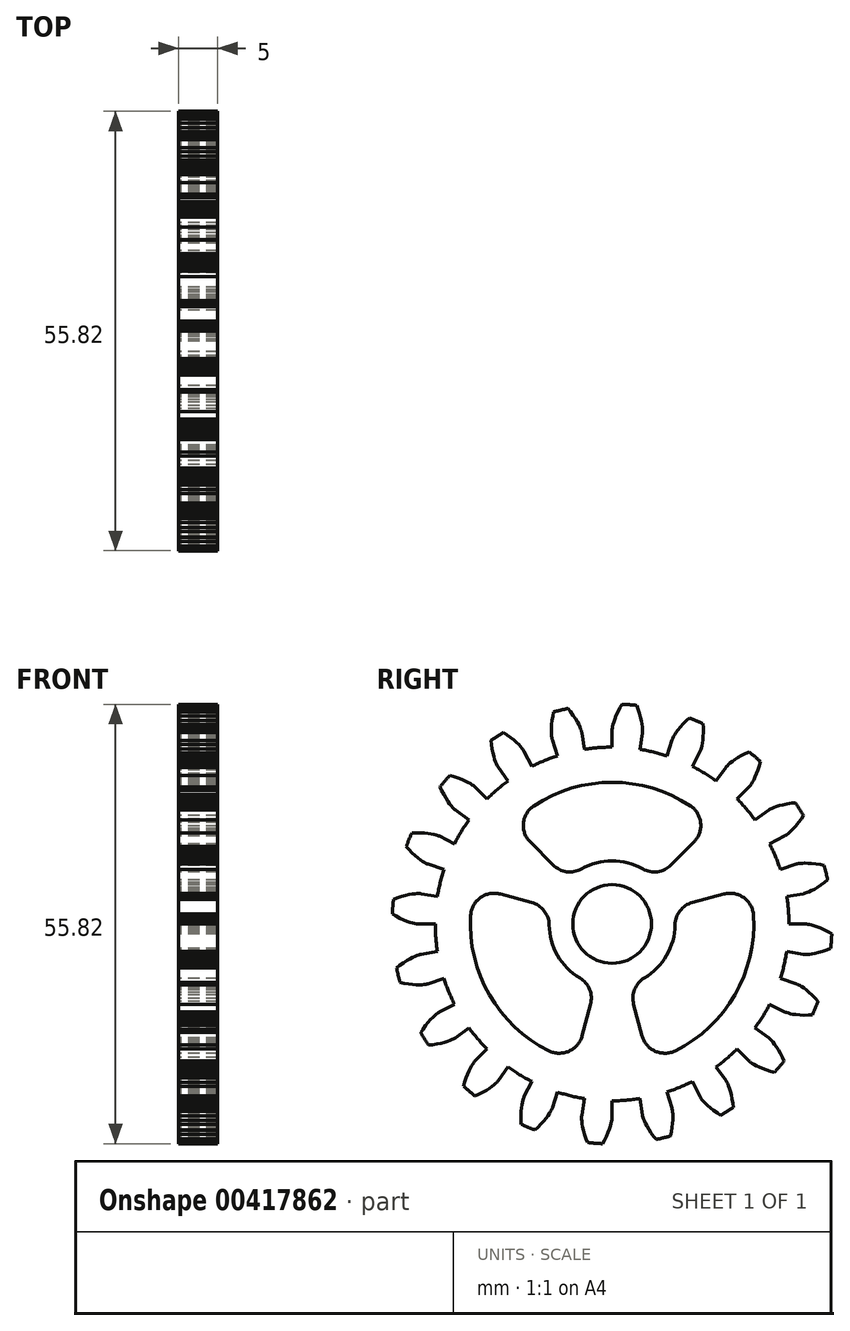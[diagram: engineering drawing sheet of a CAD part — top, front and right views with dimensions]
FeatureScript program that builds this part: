
annotation { "Feature Type Name" : "Feature", "Feature Type Description" : "" }
export const myFeature = defineFeature(function(context is Context, id is Id, definition is map)
    precondition{}
    {
        {
            assignVariable(context, id + "F0", {"name" : "GearThickness", "anyValue" : 5});
        }
        {
            var Q0;
            Q0=qCreatedBy(makeId("Right.planeOp"),FACE);
            var sketch = newSketch(context, id + "F1", { "sketchPlane" : qUnion([Q0])});
            skCircle(sketch, "E0", {"center": v(0, 0) * mm, "radius": 22.46 * mm});
            skCircle(sketch, "E1", {"center": v(0, 0) * mm, "radius": 24.6 * mm, "construction": true});
            skCircle(sketch, "E2", {"center": v(0, 0) * mm, "radius": 25.4 * mm, "construction": true});
            skCircle(sketch, "E3", {"center": v(0, 0) * mm, "radius": 27.94 * mm});
            skLineSegment(sketch, "E4", {"start": v(0, 0) * mm, "end": v(-24.6, 0) * mm, "construction": true});
            skLineSegment(sketch, "E5.1.0", {"start": v(0, 0) * mm, "end": v(-24.56, 1.23) * mm, "construction": true});
            skLineSegment(sketch, "E5.2.0", {"start": v(0, 0) * mm, "end": v(-24.47, 2.45) * mm, "construction": true});
            skLineSegment(sketch, "E5.3.0", {"start": v(0, 0) * mm, "end": v(-24.31, 3.67) * mm, "construction": true});
            skLineSegment(sketch, "E5.4.0", {"start": v(0, 0) * mm, "end": v(-24.1, 4.89) * mm, "construction": true});
            skLineSegment(sketch, "E5.5.0", {"start": v(0, 0) * mm, "end": v(-23.83, 6.08) * mm, "construction": true});
            skLineSegment(sketch, "E5.6.0", {"start": v(0, 0) * mm, "end": v(-23.5, 7.27) * mm, "construction": true});
            skLineSegment(sketch, "E5.7.0", {"start": v(0, 0) * mm, "end": v(-23.1, 8.43) * mm, "construction": true});
            skLineSegment(sketch, "E5.8.0", {"start": v(0, 0) * mm, "end": v(-22.65, 9.58) * mm, "construction": true});
            skLineSegment(sketch, "E5.9.0", {"start": v(0, 0) * mm, "end": v(-22.14, 10.7) * mm, "construction": true});
            skLineSegment(sketch, "E5.10.0", {"start": v(0, 0) * mm, "end": v(-21.58, 11.79) * mm, "construction": true});
            skLineSegment(sketch, "E5.11.0", {"start": v(0, 0) * mm, "end": v(-20.96, 12.85) * mm, "construction": true});
            skLineSegment(sketch, "E5.12.0", {"start": v(0, 0) * mm, "end": v(-20.3, 13.89) * mm, "construction": true});
            skLineSegment(sketch, "E5.13.0", {"start": v(0, 0) * mm, "end": v(-19.58, 14.88) * mm, "construction": true});
            skLineSegment(sketch, "E5.14.0", {"start": v(0, 0) * mm, "end": v(-18.8, 15.84) * mm, "construction": true});
            skLineSegment(sketch, "E5.anchor2", {"start": v(0, 0) * mm, "end": v(-18.8, 15.84) * mm, "construction": true});
            skLineSegment(sketch, "E6", {"start": v(-24.56, 1.23) * mm, "end": v(-24.62, 0) * mm, "construction": true});
            skLineSegment(sketch, "E7", {"start": v(-24.47, 2.45) * mm, "end": v(-24.71, 0) * mm, "construction": true});
            skLineSegment(sketch, "E8", {"start": v(-24.31, 3.67) * mm, "end": v(-24.87, 0.03) * mm, "construction": true});
            skLineSegment(sketch, "E9", {"start": v(-23.83, 6.08) * mm, "end": v(-25.35, 0.13) * mm, "construction": true});
            skLineSegment(sketch, "E10", {"start": v(-23.5, 7.27) * mm, "end": v(-25.67, 0.22) * mm, "construction": true});
            skLineSegment(sketch, "E11", {"start": v(-23.1, 8.43) * mm, "end": v(-26.05, 0.35) * mm, "construction": true});
            skLineSegment(sketch, "E12", {"start": v(-22.65, 9.58) * mm, "end": v(-26.48, 0.52) * mm, "construction": true});
            skLineSegment(sketch, "E13", {"start": v(-22.14, 10.7) * mm, "end": v(-26.96, 0.73) * mm, "construction": true});
            skLineSegment(sketch, "E14", {"start": v(-21.58, 11.79) * mm, "end": v(-27.48, 1) * mm, "construction": true});
            skLineSegment(sketch, "E15", {"start": v(-20.96, 12.85) * mm, "end": v(-28.03, 1.32) * mm, "construction": true});
            skLineSegment(sketch, "E16", {"start": v(-24.1, 4.89) * mm, "end": v(-25.08, 0.07) * mm, "construction": true});
            skLineSegment(sketch, "E17", {"start": v(-20.3, 13.89) * mm, "end": v(-28.63, 1.7) * mm, "construction": true});
            skLineSegment(sketch, "E18", {"start": v(-19.58, 14.88) * mm, "end": v(-29.25, 2.16) * mm, "construction": true});
            skLineSegment(sketch, "E19", {"start": v(-18.8, 15.84) * mm, "end": v(-29.9, 2.68) * mm, "construction": true});
            skLineSegment(sketch, "E20", {"start": v(0, 0) * mm, "end": v(-24.52, 1.93) * mm, "construction": true});
            skLineSegment(sketch, "E21", {"start": v(-22.46, 0) * mm, "end": v(-24.6, 0) * mm});
            skLineSegment(sketch, "E22.MirrorCS", {"start": v(-22.18, 3.51) * mm, "end": v(-24.29, 3.85) * mm});
            skLineSegment(sketch, "E23", {"start": v(-24.6, 0) * mm, "end": v(-24.62, 0) * mm});
            skLineSegment(sketch, "E24", {"start": v(-24.62, 0) * mm, "end": v(-24.71, 0) * mm});
            skLineSegment(sketch, "E25", {"start": v(-24.71, 0) * mm, "end": v(-24.87, 0.03) * mm});
            skLineSegment(sketch, "E26", {"start": v(-24.87, 0.03) * mm, "end": v(-25.08, 0.07) * mm});
            skLineSegment(sketch, "E27", {"start": v(-25.08, 0.07) * mm, "end": v(-25.35, 0.13) * mm});
            skLineSegment(sketch, "E28", {"start": v(-25.35, 0.13) * mm, "end": v(-25.67, 0.22) * mm});
            skLineSegment(sketch, "E29", {"start": v(-25.67, 0.22) * mm, "end": v(-26.05, 0.35) * mm});
            skLineSegment(sketch, "E30", {"start": v(-26.05, 0.35) * mm, "end": v(-26.48, 0.52) * mm});
            skLineSegment(sketch, "E31", {"start": v(-26.48, 0.52) * mm, "end": v(-26.96, 0.73) * mm});
            skLineSegment(sketch, "E32", {"start": v(-26.96, 0.73) * mm, "end": v(-27.48, 1) * mm});
            skLineSegment(sketch, "E33", {"start": v(-27.48, 1) * mm, "end": v(-28.03, 1.32) * mm});
            skLineSegment(sketch, "E34", {"start": v(-28.03, 1.32) * mm, "end": v(-28.63, 1.7) * mm});
            skLineSegment(sketch, "E35", {"start": v(-28.63, 1.7) * mm, "end": v(-29.25, 2.16) * mm});
            skLineSegment(sketch, "E36", {"start": v(-29.25, 2.16) * mm, "end": v(-29.9, 2.68) * mm});
            skLineSegment(sketch, "E37.MirrorCS", {"start": v(-24.29, 3.85) * mm, "end": v(-24.32, 3.85) * mm});
            skLineSegment(sketch, "E38.MirrorCS", {"start": v(-24.32, 3.85) * mm, "end": v(-24.41, 3.86) * mm});
            skLineSegment(sketch, "E39.MirrorCS", {"start": v(-24.41, 3.86) * mm, "end": v(-24.56, 3.86) * mm});
            skLineSegment(sketch, "E40.MirrorCS", {"start": v(-24.56, 3.86) * mm, "end": v(-24.78, 3.86) * mm});
            skLineSegment(sketch, "E41.MirrorCS", {"start": v(-25.06, 3.84) * mm, "end": v(-25.4, 3.8) * mm});
            skLineSegment(sketch, "E42.MirrorCS", {"start": v(-25.4, 3.8) * mm, "end": v(-25.78, 3.73) * mm});
            skLineSegment(sketch, "E43.MirrorCS", {"start": v(-25.78, 3.73) * mm, "end": v(-26.23, 3.63) * mm});
            skLineSegment(sketch, "E44.MirrorCS", {"start": v(-26.23, 3.63) * mm, "end": v(-26.74, 3.5) * mm});
            skLineSegment(sketch, "E45.MirrorCS", {"start": v(-27.3, 3.31) * mm, "end": v(-27.9, 3.08) * mm});
            skLineSegment(sketch, "E46.MirrorCS", {"start": v(-26.74, 3.5) * mm, "end": v(-27.3, 3.31) * mm});
            skLineSegment(sketch, "E47.MirrorCS", {"start": v(-27.9, 3.08) * mm, "end": v(-28.54, 2.8) * mm});
            skLineSegment(sketch, "E48.MirrorCS", {"start": v(-28.54, 2.8) * mm, "end": v(-29.23, 2.44) * mm});
            skLineSegment(sketch, "E49.MirrorCS", {"start": v(-29.23, 2.44) * mm, "end": v(-29.95, 2.03) * mm});
            skLineSegment(sketch, "E50.MirrorCS", {"start": v(-24.78, 3.86) * mm, "end": v(-25.06, 3.84) * mm});
            skLineSegment(sketch, "E51.1.0", {"start": v(-21.36, -6.94) * mm, "end": v(-23.39, -7.6) * mm});
            skLineSegment(sketch, "E51.1.1", {"start": v(-27.48, -5.7) * mm, "end": v(-28, -6.16) * mm});
            skLineSegment(sketch, "E51.1.2", {"start": v(-22.18, -3.51) * mm, "end": v(-24.29, -3.85) * mm});
            skLineSegment(sketch, "E51.1.3", {"start": v(-26.98, -5.29) * mm, "end": v(-27.48, -5.7) * mm});
            skLineSegment(sketch, "E51.1.4", {"start": v(-26.44, -7.54) * mm, "end": v(-27.07, -7.4) * mm});
            skLineSegment(sketch, "E51.1.5", {"start": v(-27.07, -7.4) * mm, "end": v(-27.75, -7.22) * mm});
            skLineSegment(sketch, "E51.1.6", {"start": v(-26.5, -4.94) * mm, "end": v(-26.98, -5.29) * mm});
            skLineSegment(sketch, "E51.1.7", {"start": v(-28.55, -6.7) * mm, "end": v(-29.11, -7.32) * mm});
            skLineSegment(sketch, "E51.1.8", {"start": v(-26.07, -4.65) * mm, "end": v(-26.5, -4.94) * mm});
            skLineSegment(sketch, "E51.1.9", {"start": v(-28.48, -6.99) * mm, "end": v(-29.26, -6.7) * mm});
            skLineSegment(sketch, "E51.1.10", {"start": v(-28, -6.16) * mm, "end": v(-28.55, -6.7) * mm});
            skLineSegment(sketch, "E51.1.11", {"start": v(-25.86, -7.63) * mm, "end": v(-26.44, -7.54) * mm});
            skLineSegment(sketch, "E51.1.12", {"start": v(-27.75, -7.22) * mm, "end": v(-28.48, -6.99) * mm});
            skLineSegment(sketch, "E51.1.13", {"start": v(-25.02, -4.1) * mm, "end": v(-25.32, -4.23) * mm});
            skLineSegment(sketch, "E51.1.14", {"start": v(-25.32, -4.23) * mm, "end": v(-25.68, -4.42) * mm});
            skLineSegment(sketch, "E51.1.15", {"start": v(-25.68, -4.42) * mm, "end": v(-26.07, -4.65) * mm});
            skLineSegment(sketch, "E51.1.16", {"start": v(-24.88, -7.72) * mm, "end": v(-25.34, -7.7) * mm});
            skLineSegment(sketch, "E51.1.17", {"start": v(-24.48, -7.72) * mm, "end": v(-24.88, -7.72) * mm});
            skLineSegment(sketch, "E51.1.18", {"start": v(-25.34, -7.7) * mm, "end": v(-25.86, -7.63) * mm});
            skLineSegment(sketch, "E51.1.19", {"start": v(-24.76, -3.99) * mm, "end": v(-25.02, -4.1) * mm});
            skLineSegment(sketch, "E51.1.20", {"start": v(-24.56, -3.92) * mm, "end": v(-24.76, -3.99) * mm});
            skLineSegment(sketch, "E51.1.21", {"start": v(-24.15, -7.71) * mm, "end": v(-24.48, -7.72) * mm});
            skLineSegment(sketch, "E51.1.22", {"start": v(-23.87, -7.69) * mm, "end": v(-24.15, -7.71) * mm});
            skLineSegment(sketch, "E51.1.23", {"start": v(-23.5, -7.63) * mm, "end": v(-23.66, -7.66) * mm});
            skLineSegment(sketch, "E51.1.24", {"start": v(-24.29, -3.85) * mm, "end": v(-24.32, -3.85) * mm});
            skLineSegment(sketch, "E51.1.25", {"start": v(-24.32, -3.85) * mm, "end": v(-24.4, -3.87) * mm});
            skLineSegment(sketch, "E51.1.26", {"start": v(-23.66, -7.66) * mm, "end": v(-23.87, -7.69) * mm});
            skLineSegment(sketch, "E51.1.27", {"start": v(-24.4, -3.87) * mm, "end": v(-24.56, -3.92) * mm});
            skLineSegment(sketch, "E51.1.28", {"start": v(-23.42, -7.6) * mm, "end": v(-23.5, -7.63) * mm});
            skLineSegment(sketch, "E51.1.29", {"start": v(-23.39, -7.6) * mm, "end": v(-23.42, -7.6) * mm});
            skLineSegment(sketch, "E51.2.0", {"start": v(-18.17, -13.2) * mm, "end": v(-19.9, -14.45) * mm});
            skLineSegment(sketch, "E51.2.1", {"start": v(-24.38, -13.9) * mm, "end": v(-24.73, -14.52) * mm});
            skLineSegment(sketch, "E51.2.2", {"start": v(-20.01, -10.2) * mm, "end": v(-21.91, -11.16) * mm});
            skLineSegment(sketch, "E51.2.3", {"start": v(-24.03, -13.36) * mm, "end": v(-24.38, -13.9) * mm});
            skLineSegment(sketch, "E51.2.4", {"start": v(-22.82, -15.34) * mm, "end": v(-23.46, -15.4) * mm});
            skLineSegment(sketch, "E51.2.5", {"start": v(-23.46, -15.4) * mm, "end": v(-24.16, -15.44) * mm});
            skLineSegment(sketch, "E51.2.6", {"start": v(-23.69, -12.89) * mm, "end": v(-24.03, -13.36) * mm});
            skLineSegment(sketch, "E51.2.7", {"start": v(-25.08, -15.2) * mm, "end": v(-25.42, -15.96) * mm});
            skLineSegment(sketch, "E51.2.8", {"start": v(-23.36, -12.48) * mm, "end": v(-23.69, -12.89) * mm});
            skLineSegment(sketch, "E51.2.9", {"start": v(-24.93, -15.45) * mm, "end": v(-25.76, -15.4) * mm});
            skLineSegment(sketch, "E51.2.10", {"start": v(-24.73, -14.52) * mm, "end": v(-25.08, -15.2) * mm});
            skLineSegment(sketch, "E51.2.11", {"start": v(-22.24, -15.25) * mm, "end": v(-22.82, -15.34) * mm});
            skLineSegment(sketch, "E51.2.12", {"start": v(-24.16, -15.44) * mm, "end": v(-24.93, -15.45) * mm});
            skLineSegment(sketch, "E51.2.13", {"start": v(-22.53, -11.62) * mm, "end": v(-22.78, -11.85) * mm});
            skLineSegment(sketch, "E51.2.14", {"start": v(-22.78, -11.85) * mm, "end": v(-23.05, -12.14) * mm});
            skLineSegment(sketch, "E51.2.15", {"start": v(-23.05, -12.14) * mm, "end": v(-23.36, -12.48) * mm});
            skLineSegment(sketch, "E51.2.16", {"start": v(-21.28, -15.03) * mm, "end": v(-21.73, -15.15) * mm});
            skLineSegment(sketch, "E51.2.17", {"start": v(-20.9, -14.91) * mm, "end": v(-21.28, -15.03) * mm});
            skLineSegment(sketch, "E51.2.18", {"start": v(-21.73, -15.15) * mm, "end": v(-22.24, -15.25) * mm});
            skLineSegment(sketch, "E51.2.19", {"start": v(-22.31, -11.44) * mm, "end": v(-22.53, -11.62) * mm});
            skLineSegment(sketch, "E51.2.20", {"start": v(-22.14, -11.31) * mm, "end": v(-22.31, -11.44) * mm});
            skLineSegment(sketch, "E51.2.21", {"start": v(-20.58, -14.8) * mm, "end": v(-20.9, -14.91) * mm});
            skLineSegment(sketch, "E51.2.22", {"start": v(-20.33, -14.69) * mm, "end": v(-20.58, -14.8) * mm});
            skLineSegment(sketch, "E51.2.23", {"start": v(-20, -14.52) * mm, "end": v(-20.13, -14.6) * mm});
            skLineSegment(sketch, "E51.2.24", {"start": v(-21.91, -11.16) * mm, "end": v(-21.94, -11.18) * mm});
            skLineSegment(sketch, "E51.2.25", {"start": v(-21.94, -11.18) * mm, "end": v(-22.02, -11.23) * mm});
            skLineSegment(sketch, "E51.2.26", {"start": v(-20.13, -14.6) * mm, "end": v(-20.33, -14.69) * mm});
            skLineSegment(sketch, "E51.2.27", {"start": v(-22.02, -11.23) * mm, "end": v(-22.14, -11.31) * mm});
            skLineSegment(sketch, "E51.2.28", {"start": v(-19.92, -14.47) * mm, "end": v(-20, -14.52) * mm});
            skLineSegment(sketch, "E51.2.29", {"start": v(-19.9, -14.45) * mm, "end": v(-19.92, -14.47) * mm});
            skLineSegment(sketch, "E51.3.0", {"start": v(-13.2, -18.17) * mm, "end": v(-14.45, -19.9) * mm});
            skLineSegment(sketch, "E51.3.1", {"start": v(-18.89, -20.76) * mm, "end": v(-19.03, -21.45) * mm});
            skLineSegment(sketch, "E51.3.2", {"start": v(-15.88, -15.88) * mm, "end": v(-17.39, -17.39) * mm});
            skLineSegment(sketch, "E51.3.3", {"start": v(-18.72, -20.13) * mm, "end": v(-18.89, -20.76) * mm});
            skLineSegment(sketch, "E51.3.4", {"start": v(-16.96, -21.64) * mm, "end": v(-17.55, -21.9) * mm});
            skLineSegment(sketch, "E51.3.5", {"start": v(-17.55, -21.9) * mm, "end": v(-18.2, -22.16) * mm});
            skLineSegment(sketch, "E51.3.6", {"start": v(-18.54, -19.58) * mm, "end": v(-18.72, -20.13) * mm});
            skLineSegment(sketch, "E51.3.7", {"start": v(-19.16, -22.2) * mm, "end": v(-19.25, -23.03) * mm});
            skLineSegment(sketch, "E51.3.8", {"start": v(-18.36, -19.09) * mm, "end": v(-18.54, -19.58) * mm});
            skLineSegment(sketch, "E51.3.9", {"start": v(-18.94, -22.4) * mm, "end": v(-19.74, -22.61) * mm});
            skLineSegment(sketch, "E51.3.10", {"start": v(-19.03, -21.45) * mm, "end": v(-19.16, -22.2) * mm});
            skLineSegment(sketch, "E51.3.11", {"start": v(-16.44, -21.38) * mm, "end": v(-16.96, -21.64) * mm});
            skLineSegment(sketch, "E51.3.12", {"start": v(-18.2, -22.16) * mm, "end": v(-18.94, -22.4) * mm});
            skLineSegment(sketch, "E51.3.13", {"start": v(-17.83, -18.01) * mm, "end": v(-18, -18.3) * mm});
            skLineSegment(sketch, "E51.3.14", {"start": v(-18, -18.3) * mm, "end": v(-18.18, -18.67) * mm});
            skLineSegment(sketch, "E51.3.15", {"start": v(-18.18, -18.67) * mm, "end": v(-18.36, -19.09) * mm});
            skLineSegment(sketch, "E51.3.16", {"start": v(-15.6, -20.87) * mm, "end": v(-15.98, -21.12) * mm});
            skLineSegment(sketch, "E51.3.17", {"start": v(-15.27, -20.64) * mm, "end": v(-15.6, -20.87) * mm});
            skLineSegment(sketch, "E51.3.18", {"start": v(-15.98, -21.12) * mm, "end": v(-16.44, -21.38) * mm});
            skLineSegment(sketch, "E51.3.19", {"start": v(-17.69, -17.78) * mm, "end": v(-17.83, -18.01) * mm});
            skLineSegment(sketch, "E51.3.20", {"start": v(-17.56, -17.6) * mm, "end": v(-17.69, -17.78) * mm});
            skLineSegment(sketch, "E51.3.21", {"start": v(-15, -20.43) * mm, "end": v(-15.27, -20.64) * mm});
            skLineSegment(sketch, "E51.3.22", {"start": v(-14.8, -20.25) * mm, "end": v(-15, -20.43) * mm});
            skLineSegment(sketch, "E51.3.23", {"start": v(-14.53, -19.99) * mm, "end": v(-14.64, -20.1) * mm});
            skLineSegment(sketch, "E51.3.24", {"start": v(-17.39, -17.39) * mm, "end": v(-17.4, -17.41) * mm});
            skLineSegment(sketch, "E51.3.25", {"start": v(-17.4, -17.41) * mm, "end": v(-17.47, -17.48) * mm});
            skLineSegment(sketch, "E51.3.26", {"start": v(-14.64, -20.1) * mm, "end": v(-14.8, -20.25) * mm});
            skLineSegment(sketch, "E51.3.27", {"start": v(-17.47, -17.48) * mm, "end": v(-17.56, -17.6) * mm});
            skLineSegment(sketch, "E51.3.28", {"start": v(-14.47, -19.92) * mm, "end": v(-14.53, -19.99) * mm});
            skLineSegment(sketch, "E51.3.29", {"start": v(-14.45, -19.9) * mm, "end": v(-14.47, -19.92) * mm});
            skLineSegment(sketch, "E51.4.0", {"start": v(-6.94, -21.36) * mm, "end": v(-7.6, -23.39) * mm});
            skLineSegment(sketch, "E51.4.1", {"start": v(-11.55, -25.58) * mm, "end": v(-11.47, -26.28) * mm});
            skLineSegment(sketch, "E51.4.2", {"start": v(-10.2, -20.01) * mm, "end": v(-11.16, -21.91) * mm});
            skLineSegment(sketch, "E51.4.3", {"start": v(-11.58, -24.93) * mm, "end": v(-11.55, -25.58) * mm});
            skLineSegment(sketch, "E51.4.4", {"start": v(-9.44, -25.82) * mm, "end": v(-9.92, -26.25) * mm});
            skLineSegment(sketch, "E51.4.5", {"start": v(-9.92, -26.25) * mm, "end": v(-10.47, -26.7) * mm});
            skLineSegment(sketch, "E51.4.6", {"start": v(-11.59, -24.35) * mm, "end": v(-11.58, -24.93) * mm});
            skLineSegment(sketch, "E51.4.7", {"start": v(-11.36, -27.04) * mm, "end": v(-11.19, -27.85) * mm});
            skLineSegment(sketch, "E51.4.8", {"start": v(-11.56, -23.83) * mm, "end": v(-11.59, -24.35) * mm});
            skLineSegment(sketch, "E51.4.9", {"start": v(-11.1, -27.15) * mm, "end": v(-11.78, -27.6) * mm});
            skLineSegment(sketch, "E51.4.10", {"start": v(-11.47, -26.28) * mm, "end": v(-11.36, -27.04) * mm});
            skLineSegment(sketch, "E51.4.11", {"start": v(-9.03, -25.41) * mm, "end": v(-9.44, -25.82) * mm});
            skLineSegment(sketch, "E51.4.12", {"start": v(-10.47, -26.7) * mm, "end": v(-11.1, -27.15) * mm});
            skLineSegment(sketch, "E51.4.13", {"start": v(-11.4, -22.64) * mm, "end": v(-11.46, -22.97) * mm});
            skLineSegment(sketch, "E51.4.14", {"start": v(-11.46, -22.97) * mm, "end": v(-11.52, -23.37) * mm});
            skLineSegment(sketch, "E51.4.15", {"start": v(-11.52, -23.37) * mm, "end": v(-11.56, -23.83) * mm});
            skLineSegment(sketch, "E51.4.16", {"start": v(-8.38, -24.67) * mm, "end": v(-8.67, -25.02) * mm});
            skLineSegment(sketch, "E51.4.17", {"start": v(-8.14, -24.35) * mm, "end": v(-8.38, -24.67) * mm});
            skLineSegment(sketch, "E51.4.18", {"start": v(-8.67, -25.02) * mm, "end": v(-9.03, -25.41) * mm});
            skLineSegment(sketch, "E51.4.19", {"start": v(-11.33, -22.37) * mm, "end": v(-11.4, -22.64) * mm});
            skLineSegment(sketch, "E51.4.20", {"start": v(-11.26, -22.17) * mm, "end": v(-11.33, -22.37) * mm});
            skLineSegment(sketch, "E51.4.21", {"start": v(-7.95, -24.07) * mm, "end": v(-8.14, -24.35) * mm});
            skLineSegment(sketch, "E51.4.22", {"start": v(-7.81, -23.83) * mm, "end": v(-7.95, -24.07) * mm});
            skLineSegment(sketch, "E51.4.23", {"start": v(-7.64, -23.5) * mm, "end": v(-7.71, -23.64) * mm});
            skLineSegment(sketch, "E51.4.24", {"start": v(-11.16, -21.91) * mm, "end": v(-11.18, -21.94) * mm});
            skLineSegment(sketch, "E51.4.25", {"start": v(-11.18, -21.94) * mm, "end": v(-11.21, -22.02) * mm});
            skLineSegment(sketch, "E51.4.26", {"start": v(-7.71, -23.64) * mm, "end": v(-7.81, -23.83) * mm});
            skLineSegment(sketch, "E51.4.27", {"start": v(-11.21, -22.02) * mm, "end": v(-11.26, -22.17) * mm});
            skLineSegment(sketch, "E51.4.28", {"start": v(-7.6, -23.42) * mm, "end": v(-7.64, -23.5) * mm});
            skLineSegment(sketch, "E51.4.29", {"start": v(-7.6, -23.39) * mm, "end": v(-7.6, -23.42) * mm});
            skLineSegment(sketch, "E51.5.0", {"start": v(0, -22.46) * mm, "end": v(0, -24.6) * mm});
            skLineSegment(sketch, "E51.5.1", {"start": v(-3.08, -27.9) * mm, "end": v(-2.8, -28.54) * mm});
            skLineSegment(sketch, "E51.5.2", {"start": v(-3.51, -22.18) * mm, "end": v(-3.85, -24.29) * mm});
            skLineSegment(sketch, "E51.5.3", {"start": v(-3.31, -27.3) * mm, "end": v(-3.08, -27.9) * mm});
            skLineSegment(sketch, "E51.5.4", {"start": v(-1, -27.48) * mm, "end": v(-1.32, -28.03) * mm});
            skLineSegment(sketch, "E51.5.5", {"start": v(-1.32, -28.03) * mm, "end": v(-1.7, -28.63) * mm});
            skLineSegment(sketch, "E51.5.6", {"start": v(-3.5, -26.74) * mm, "end": v(-3.31, -27.3) * mm});
            skLineSegment(sketch, "E51.5.7", {"start": v(-2.44, -29.23) * mm, "end": v(-2.03, -29.95) * mm});
            skLineSegment(sketch, "E51.5.8", {"start": v(-3.63, -26.23) * mm, "end": v(-3.5, -26.74) * mm});
            skLineSegment(sketch, "E51.5.9", {"start": v(-2.16, -29.25) * mm, "end": v(-2.68, -29.9) * mm});
            skLineSegment(sketch, "E51.5.10", {"start": v(-2.8, -28.54) * mm, "end": v(-2.44, -29.23) * mm});
            skLineSegment(sketch, "E51.5.11", {"start": v(-0.73, -26.96) * mm, "end": v(-1, -27.48) * mm});
            skLineSegment(sketch, "E51.5.12", {"start": v(-1.7, -28.63) * mm, "end": v(-2.16, -29.25) * mm});
            skLineSegment(sketch, "E51.5.13", {"start": v(-3.84, -25.06) * mm, "end": v(-3.8, -25.4) * mm});
            skLineSegment(sketch, "E51.5.14", {"start": v(-3.8, -25.4) * mm, "end": v(-3.73, -25.78) * mm});
            skLineSegment(sketch, "E51.5.15", {"start": v(-3.73, -25.78) * mm, "end": v(-3.63, -26.23) * mm});
            skLineSegment(sketch, "E51.5.16", {"start": v(-0.35, -26.05) * mm, "end": v(-0.52, -26.48) * mm});
            skLineSegment(sketch, "E51.5.17", {"start": v(-0.22, -25.67) * mm, "end": v(-0.35, -26.05) * mm});
            skLineSegment(sketch, "E51.5.18", {"start": v(-0.52, -26.48) * mm, "end": v(-0.73, -26.96) * mm});
            skLineSegment(sketch, "E51.5.19", {"start": v(-3.86, -24.78) * mm, "end": v(-3.84, -25.06) * mm});
            skLineSegment(sketch, "E51.5.20", {"start": v(-3.86, -24.56) * mm, "end": v(-3.86, -24.78) * mm});
            skLineSegment(sketch, "E51.5.21", {"start": v(-0.13, -25.35) * mm, "end": v(-0.22, -25.67) * mm});
            skLineSegment(sketch, "E51.5.22", {"start": v(-0.07, -25.08) * mm, "end": v(-0.13, -25.35) * mm});
            skLineSegment(sketch, "E51.5.23", {"start": v(0, -24.71) * mm, "end": v(-0.03, -24.87) * mm});
            skLineSegment(sketch, "E51.5.24", {"start": v(-3.85, -24.29) * mm, "end": v(-3.85, -24.32) * mm});
            skLineSegment(sketch, "E51.5.25", {"start": v(-3.85, -24.32) * mm, "end": v(-3.86, -24.41) * mm});
            skLineSegment(sketch, "E51.5.26", {"start": v(-0.03, -24.87) * mm, "end": v(-0.07, -25.08) * mm});
            skLineSegment(sketch, "E51.5.27", {"start": v(-3.86, -24.41) * mm, "end": v(-3.86, -24.56) * mm});
            skLineSegment(sketch, "E51.5.28", {"start": v(0, -24.62) * mm, "end": v(0, -24.71) * mm});
            skLineSegment(sketch, "E51.5.29", {"start": v(0, -24.6) * mm, "end": v(0, -24.62) * mm});
            skLineSegment(sketch, "E51.6.0", {"start": v(6.94, -21.36) * mm, "end": v(7.6, -23.39) * mm});
            skLineSegment(sketch, "E51.6.1", {"start": v(5.7, -27.48) * mm, "end": v(6.16, -28) * mm});
            skLineSegment(sketch, "E51.6.2", {"start": v(3.51, -22.18) * mm, "end": v(3.85, -24.29) * mm});
            skLineSegment(sketch, "E51.6.3", {"start": v(5.29, -26.98) * mm, "end": v(5.7, -27.48) * mm});
            skLineSegment(sketch, "E51.6.4", {"start": v(7.54, -26.44) * mm, "end": v(7.4, -27.07) * mm});
            skLineSegment(sketch, "E51.6.5", {"start": v(7.4, -27.07) * mm, "end": v(7.22, -27.75) * mm});
            skLineSegment(sketch, "E51.6.6", {"start": v(4.94, -26.5) * mm, "end": v(5.29, -26.98) * mm});
            skLineSegment(sketch, "E51.6.7", {"start": v(6.7, -28.55) * mm, "end": v(7.32, -29.11) * mm});
            skLineSegment(sketch, "E51.6.8", {"start": v(4.65, -26.07) * mm, "end": v(4.94, -26.5) * mm});
            skLineSegment(sketch, "E51.6.9", {"start": v(6.99, -28.48) * mm, "end": v(6.7, -29.26) * mm});
            skLineSegment(sketch, "E51.6.10", {"start": v(6.16, -28) * mm, "end": v(6.7, -28.55) * mm});
            skLineSegment(sketch, "E51.6.11", {"start": v(7.63, -25.86) * mm, "end": v(7.54, -26.44) * mm});
            skLineSegment(sketch, "E51.6.12", {"start": v(7.22, -27.75) * mm, "end": v(6.99, -28.48) * mm});
            skLineSegment(sketch, "E51.6.13", {"start": v(4.1, -25.02) * mm, "end": v(4.23, -25.32) * mm});
            skLineSegment(sketch, "E51.6.14", {"start": v(4.23, -25.32) * mm, "end": v(4.42, -25.68) * mm});
            skLineSegment(sketch, "E51.6.15", {"start": v(4.42, -25.68) * mm, "end": v(4.65, -26.07) * mm});
            skLineSegment(sketch, "E51.6.16", {"start": v(7.72, -24.88) * mm, "end": v(7.7, -25.34) * mm});
            skLineSegment(sketch, "E51.6.17", {"start": v(7.72, -24.48) * mm, "end": v(7.72, -24.88) * mm});
            skLineSegment(sketch, "E51.6.18", {"start": v(7.7, -25.34) * mm, "end": v(7.63, -25.86) * mm});
            skLineSegment(sketch, "E51.6.19", {"start": v(3.99, -24.76) * mm, "end": v(4.1, -25.02) * mm});
            skLineSegment(sketch, "E51.6.20", {"start": v(3.92, -24.56) * mm, "end": v(3.99, -24.76) * mm});
            skLineSegment(sketch, "E51.6.21", {"start": v(7.71, -24.15) * mm, "end": v(7.72, -24.48) * mm});
            skLineSegment(sketch, "E51.6.22", {"start": v(7.69, -23.87) * mm, "end": v(7.71, -24.15) * mm});
            skLineSegment(sketch, "E51.6.23", {"start": v(7.63, -23.5) * mm, "end": v(7.66, -23.66) * mm});
            skLineSegment(sketch, "E51.6.24", {"start": v(3.85, -24.29) * mm, "end": v(3.85, -24.32) * mm});
            skLineSegment(sketch, "E51.6.25", {"start": v(3.85, -24.32) * mm, "end": v(3.87, -24.4) * mm});
            skLineSegment(sketch, "E51.6.26", {"start": v(7.66, -23.66) * mm, "end": v(7.69, -23.87) * mm});
            skLineSegment(sketch, "E51.6.27", {"start": v(3.87, -24.4) * mm, "end": v(3.92, -24.56) * mm});
            skLineSegment(sketch, "E51.6.28", {"start": v(7.6, -23.42) * mm, "end": v(7.63, -23.5) * mm});
            skLineSegment(sketch, "E51.6.29", {"start": v(7.6, -23.39) * mm, "end": v(7.6, -23.42) * mm});
            skLineSegment(sketch, "E51.7.0", {"start": v(13.2, -18.17) * mm, "end": v(14.45, -19.9) * mm});
            skLineSegment(sketch, "E51.7.1", {"start": v(13.9, -24.38) * mm, "end": v(14.52, -24.73) * mm});
            skLineSegment(sketch, "E51.7.2", {"start": v(10.2, -20.01) * mm, "end": v(11.16, -21.91) * mm});
            skLineSegment(sketch, "E51.7.3", {"start": v(13.36, -24.03) * mm, "end": v(13.9, -24.38) * mm});
            skLineSegment(sketch, "E51.7.4", {"start": v(15.34, -22.82) * mm, "end": v(15.4, -23.46) * mm});
            skLineSegment(sketch, "E51.7.5", {"start": v(15.4, -23.46) * mm, "end": v(15.44, -24.16) * mm});
            skLineSegment(sketch, "E51.7.6", {"start": v(12.89, -23.69) * mm, "end": v(13.36, -24.03) * mm});
            skLineSegment(sketch, "E51.7.7", {"start": v(15.2, -25.08) * mm, "end": v(15.96, -25.42) * mm});
            skLineSegment(sketch, "E51.7.8", {"start": v(12.48, -23.36) * mm, "end": v(12.89, -23.69) * mm});
            skLineSegment(sketch, "E51.7.9", {"start": v(15.45, -24.93) * mm, "end": v(15.4, -25.76) * mm});
            skLineSegment(sketch, "E51.7.10", {"start": v(14.52, -24.73) * mm, "end": v(15.2, -25.08) * mm});
            skLineSegment(sketch, "E51.7.11", {"start": v(15.25, -22.24) * mm, "end": v(15.34, -22.82) * mm});
            skLineSegment(sketch, "E51.7.12", {"start": v(15.44, -24.16) * mm, "end": v(15.45, -24.93) * mm});
            skLineSegment(sketch, "E51.7.13", {"start": v(11.62, -22.53) * mm, "end": v(11.85, -22.78) * mm});
            skLineSegment(sketch, "E51.7.14", {"start": v(11.85, -22.78) * mm, "end": v(12.14, -23.05) * mm});
            skLineSegment(sketch, "E51.7.15", {"start": v(12.14, -23.05) * mm, "end": v(12.48, -23.36) * mm});
            skLineSegment(sketch, "E51.7.16", {"start": v(15.03, -21.28) * mm, "end": v(15.15, -21.73) * mm});
            skLineSegment(sketch, "E51.7.17", {"start": v(14.91, -20.9) * mm, "end": v(15.03, -21.28) * mm});
            skLineSegment(sketch, "E51.7.18", {"start": v(15.15, -21.73) * mm, "end": v(15.25, -22.24) * mm});
            skLineSegment(sketch, "E51.7.19", {"start": v(11.44, -22.31) * mm, "end": v(11.62, -22.53) * mm});
            skLineSegment(sketch, "E51.7.20", {"start": v(11.31, -22.14) * mm, "end": v(11.44, -22.31) * mm});
            skLineSegment(sketch, "E51.7.21", {"start": v(14.8, -20.58) * mm, "end": v(14.91, -20.9) * mm});
            skLineSegment(sketch, "E51.7.22", {"start": v(14.69, -20.33) * mm, "end": v(14.8, -20.58) * mm});
            skLineSegment(sketch, "E51.7.23", {"start": v(14.52, -20) * mm, "end": v(14.6, -20.13) * mm});
            skLineSegment(sketch, "E51.7.24", {"start": v(11.16, -21.91) * mm, "end": v(11.18, -21.94) * mm});
            skLineSegment(sketch, "E51.7.25", {"start": v(11.18, -21.94) * mm, "end": v(11.23, -22.02) * mm});
            skLineSegment(sketch, "E51.7.26", {"start": v(14.6, -20.13) * mm, "end": v(14.69, -20.33) * mm});
            skLineSegment(sketch, "E51.7.27", {"start": v(11.23, -22.02) * mm, "end": v(11.31, -22.14) * mm});
            skLineSegment(sketch, "E51.7.28", {"start": v(14.47, -19.92) * mm, "end": v(14.52, -20) * mm});
            skLineSegment(sketch, "E51.7.29", {"start": v(14.45, -19.9) * mm, "end": v(14.47, -19.92) * mm});
            skLineSegment(sketch, "E51.8.0", {"start": v(18.17, -13.2) * mm, "end": v(19.9, -14.45) * mm});
            skLineSegment(sketch, "E51.8.1", {"start": v(20.76, -18.89) * mm, "end": v(21.45, -19.03) * mm});
            skLineSegment(sketch, "E51.8.2", {"start": v(15.88, -15.88) * mm, "end": v(17.39, -17.39) * mm});
            skLineSegment(sketch, "E51.8.3", {"start": v(20.13, -18.72) * mm, "end": v(20.76, -18.89) * mm});
            skLineSegment(sketch, "E51.8.4", {"start": v(21.64, -16.96) * mm, "end": v(21.9, -17.55) * mm});
            skLineSegment(sketch, "E51.8.5", {"start": v(21.9, -17.55) * mm, "end": v(22.16, -18.2) * mm});
            skLineSegment(sketch, "E51.8.6", {"start": v(19.58, -18.54) * mm, "end": v(20.13, -18.72) * mm});
            skLineSegment(sketch, "E51.8.7", {"start": v(22.2, -19.16) * mm, "end": v(23.03, -19.25) * mm});
            skLineSegment(sketch, "E51.8.8", {"start": v(19.09, -18.36) * mm, "end": v(19.58, -18.54) * mm});
            skLineSegment(sketch, "E51.8.9", {"start": v(22.4, -18.94) * mm, "end": v(22.61, -19.74) * mm});
            skLineSegment(sketch, "E51.8.10", {"start": v(21.45, -19.03) * mm, "end": v(22.2, -19.16) * mm});
            skLineSegment(sketch, "E51.8.11", {"start": v(21.38, -16.44) * mm, "end": v(21.64, -16.96) * mm});
            skLineSegment(sketch, "E51.8.12", {"start": v(22.16, -18.2) * mm, "end": v(22.4, -18.94) * mm});
            skLineSegment(sketch, "E51.8.13", {"start": v(18.01, -17.83) * mm, "end": v(18.3, -18) * mm});
            skLineSegment(sketch, "E51.8.14", {"start": v(18.3, -18) * mm, "end": v(18.67, -18.18) * mm});
            skLineSegment(sketch, "E51.8.15", {"start": v(18.67, -18.18) * mm, "end": v(19.09, -18.36) * mm});
            skLineSegment(sketch, "E51.8.16", {"start": v(20.87, -15.6) * mm, "end": v(21.12, -15.98) * mm});
            skLineSegment(sketch, "E51.8.17", {"start": v(20.64, -15.27) * mm, "end": v(20.87, -15.6) * mm});
            skLineSegment(sketch, "E51.8.18", {"start": v(21.12, -15.98) * mm, "end": v(21.38, -16.44) * mm});
            skLineSegment(sketch, "E51.8.19", {"start": v(17.78, -17.69) * mm, "end": v(18.01, -17.83) * mm});
            skLineSegment(sketch, "E51.8.20", {"start": v(17.6, -17.56) * mm, "end": v(17.78, -17.69) * mm});
            skLineSegment(sketch, "E51.8.21", {"start": v(20.43, -15) * mm, "end": v(20.64, -15.27) * mm});
            skLineSegment(sketch, "E51.8.22", {"start": v(20.25, -14.8) * mm, "end": v(20.43, -15) * mm});
            skLineSegment(sketch, "E51.8.23", {"start": v(19.99, -14.53) * mm, "end": v(20.1, -14.64) * mm});
            skLineSegment(sketch, "E51.8.24", {"start": v(17.39, -17.39) * mm, "end": v(17.41, -17.4) * mm});
            skLineSegment(sketch, "E51.8.25", {"start": v(17.41, -17.4) * mm, "end": v(17.48, -17.47) * mm});
            skLineSegment(sketch, "E51.8.26", {"start": v(20.1, -14.64) * mm, "end": v(20.25, -14.8) * mm});
            skLineSegment(sketch, "E51.8.27", {"start": v(17.48, -17.47) * mm, "end": v(17.6, -17.56) * mm});
            skLineSegment(sketch, "E51.8.28", {"start": v(19.92, -14.47) * mm, "end": v(19.99, -14.53) * mm});
            skLineSegment(sketch, "E51.8.29", {"start": v(19.9, -14.45) * mm, "end": v(19.92, -14.47) * mm});
            skLineSegment(sketch, "E51.9.0", {"start": v(21.36, -6.94) * mm, "end": v(23.39, -7.6) * mm});
            skLineSegment(sketch, "E51.9.1", {"start": v(25.58, -11.55) * mm, "end": v(26.28, -11.47) * mm});
            skLineSegment(sketch, "E51.9.2", {"start": v(20.01, -10.2) * mm, "end": v(21.91, -11.16) * mm});
            skLineSegment(sketch, "E51.9.3", {"start": v(24.93, -11.58) * mm, "end": v(25.58, -11.55) * mm});
            skLineSegment(sketch, "E51.9.4", {"start": v(25.82, -9.44) * mm, "end": v(26.25, -9.92) * mm});
            skLineSegment(sketch, "E51.9.5", {"start": v(26.25, -9.92) * mm, "end": v(26.7, -10.47) * mm});
            skLineSegment(sketch, "E51.9.6", {"start": v(24.35, -11.59) * mm, "end": v(24.93, -11.58) * mm});
            skLineSegment(sketch, "E51.9.7", {"start": v(27.04, -11.36) * mm, "end": v(27.85, -11.19) * mm});
            skLineSegment(sketch, "E51.9.8", {"start": v(23.83, -11.56) * mm, "end": v(24.35, -11.59) * mm});
            skLineSegment(sketch, "E51.9.9", {"start": v(27.15, -11.1) * mm, "end": v(27.6, -11.78) * mm});
            skLineSegment(sketch, "E51.9.10", {"start": v(26.28, -11.47) * mm, "end": v(27.04, -11.36) * mm});
            skLineSegment(sketch, "E51.9.11", {"start": v(25.41, -9.03) * mm, "end": v(25.82, -9.44) * mm});
            skLineSegment(sketch, "E51.9.12", {"start": v(26.7, -10.47) * mm, "end": v(27.15, -11.1) * mm});
            skLineSegment(sketch, "E51.9.13", {"start": v(22.64, -11.4) * mm, "end": v(22.97, -11.46) * mm});
            skLineSegment(sketch, "E51.9.14", {"start": v(22.97, -11.46) * mm, "end": v(23.37, -11.52) * mm});
            skLineSegment(sketch, "E51.9.15", {"start": v(23.37, -11.52) * mm, "end": v(23.83, -11.56) * mm});
            skLineSegment(sketch, "E51.9.16", {"start": v(24.67, -8.38) * mm, "end": v(25.02, -8.67) * mm});
            skLineSegment(sketch, "E51.9.17", {"start": v(24.35, -8.14) * mm, "end": v(24.67, -8.38) * mm});
            skLineSegment(sketch, "E51.9.18", {"start": v(25.02, -8.67) * mm, "end": v(25.41, -9.03) * mm});
            skLineSegment(sketch, "E51.9.19", {"start": v(22.37, -11.33) * mm, "end": v(22.64, -11.4) * mm});
            skLineSegment(sketch, "E51.9.20", {"start": v(22.17, -11.26) * mm, "end": v(22.37, -11.33) * mm});
            skLineSegment(sketch, "E51.9.21", {"start": v(24.07, -7.95) * mm, "end": v(24.35, -8.14) * mm});
            skLineSegment(sketch, "E51.9.22", {"start": v(23.83, -7.81) * mm, "end": v(24.07, -7.95) * mm});
            skLineSegment(sketch, "E51.9.23", {"start": v(23.5, -7.64) * mm, "end": v(23.64, -7.71) * mm});
            skLineSegment(sketch, "E51.9.24", {"start": v(21.91, -11.16) * mm, "end": v(21.94, -11.18) * mm});
            skLineSegment(sketch, "E51.9.25", {"start": v(21.94, -11.18) * mm, "end": v(22.02, -11.21) * mm});
            skLineSegment(sketch, "E51.9.26", {"start": v(23.64, -7.71) * mm, "end": v(23.83, -7.81) * mm});
            skLineSegment(sketch, "E51.9.27", {"start": v(22.02, -11.21) * mm, "end": v(22.17, -11.26) * mm});
            skLineSegment(sketch, "E51.9.28", {"start": v(23.42, -7.6) * mm, "end": v(23.5, -7.64) * mm});
            skLineSegment(sketch, "E51.9.29", {"start": v(23.39, -7.6) * mm, "end": v(23.42, -7.6) * mm});
            skLineSegment(sketch, "E51.10.0", {"start": v(22.46, 0) * mm, "end": v(24.6, 0) * mm});
            skLineSegment(sketch, "E51.10.1", {"start": v(27.9, -3.08) * mm, "end": v(28.54, -2.8) * mm});
            skLineSegment(sketch, "E51.10.2", {"start": v(22.18, -3.51) * mm, "end": v(24.29, -3.85) * mm});
            skLineSegment(sketch, "E51.10.3", {"start": v(27.3, -3.31) * mm, "end": v(27.9, -3.08) * mm});
            skLineSegment(sketch, "E51.10.4", {"start": v(27.48, -1) * mm, "end": v(28.03, -1.32) * mm});
            skLineSegment(sketch, "E51.10.5", {"start": v(28.03, -1.32) * mm, "end": v(28.63, -1.7) * mm});
            skLineSegment(sketch, "E51.10.6", {"start": v(26.74, -3.5) * mm, "end": v(27.3, -3.31) * mm});
            skLineSegment(sketch, "E51.10.7", {"start": v(29.23, -2.44) * mm, "end": v(29.95, -2.03) * mm});
            skLineSegment(sketch, "E51.10.8", {"start": v(26.23, -3.63) * mm, "end": v(26.74, -3.5) * mm});
            skLineSegment(sketch, "E51.10.9", {"start": v(29.25, -2.16) * mm, "end": v(29.9, -2.68) * mm});
            skLineSegment(sketch, "E51.10.10", {"start": v(28.54, -2.8) * mm, "end": v(29.23, -2.44) * mm});
            skLineSegment(sketch, "E51.10.11", {"start": v(26.96, -0.73) * mm, "end": v(27.48, -1) * mm});
            skLineSegment(sketch, "E51.10.12", {"start": v(28.63, -1.7) * mm, "end": v(29.25, -2.16) * mm});
            skLineSegment(sketch, "E51.10.13", {"start": v(25.06, -3.84) * mm, "end": v(25.4, -3.8) * mm});
            skLineSegment(sketch, "E51.10.14", {"start": v(25.4, -3.8) * mm, "end": v(25.78, -3.73) * mm});
            skLineSegment(sketch, "E51.10.15", {"start": v(25.78, -3.73) * mm, "end": v(26.23, -3.63) * mm});
            skLineSegment(sketch, "E51.10.16", {"start": v(26.05, -0.35) * mm, "end": v(26.48, -0.52) * mm});
            skLineSegment(sketch, "E51.10.17", {"start": v(25.67, -0.22) * mm, "end": v(26.05, -0.35) * mm});
            skLineSegment(sketch, "E51.10.18", {"start": v(26.48, -0.52) * mm, "end": v(26.96, -0.73) * mm});
            skLineSegment(sketch, "E51.10.19", {"start": v(24.78, -3.86) * mm, "end": v(25.06, -3.84) * mm});
            skLineSegment(sketch, "E51.10.20", {"start": v(24.56, -3.86) * mm, "end": v(24.78, -3.86) * mm});
            skLineSegment(sketch, "E51.10.21", {"start": v(25.35, -0.13) * mm, "end": v(25.67, -0.22) * mm});
            skLineSegment(sketch, "E51.10.22", {"start": v(25.08, -0.07) * mm, "end": v(25.35, -0.13) * mm});
            skLineSegment(sketch, "E51.10.23", {"start": v(24.71, 0) * mm, "end": v(24.87, -0.03) * mm});
            skLineSegment(sketch, "E51.10.24", {"start": v(24.29, -3.85) * mm, "end": v(24.32, -3.85) * mm});
            skLineSegment(sketch, "E51.10.25", {"start": v(24.32, -3.85) * mm, "end": v(24.41, -3.86) * mm});
            skLineSegment(sketch, "E51.10.26", {"start": v(24.87, -0.03) * mm, "end": v(25.08, -0.07) * mm});
            skLineSegment(sketch, "E51.10.27", {"start": v(24.41, -3.86) * mm, "end": v(24.56, -3.86) * mm});
            skLineSegment(sketch, "E51.10.28", {"start": v(24.62, 0) * mm, "end": v(24.71, 0) * mm});
            skLineSegment(sketch, "E51.10.29", {"start": v(24.6, 0) * mm, "end": v(24.62, 0) * mm});
            skLineSegment(sketch, "E51.11.0", {"start": v(21.36, 6.94) * mm, "end": v(23.39, 7.6) * mm});
            skLineSegment(sketch, "E51.11.1", {"start": v(27.48, 5.7) * mm, "end": v(28, 6.16) * mm});
            skLineSegment(sketch, "E51.11.2", {"start": v(22.18, 3.51) * mm, "end": v(24.29, 3.85) * mm});
            skLineSegment(sketch, "E51.11.3", {"start": v(26.98, 5.29) * mm, "end": v(27.48, 5.7) * mm});
            skLineSegment(sketch, "E51.11.4", {"start": v(26.44, 7.54) * mm, "end": v(27.07, 7.4) * mm});
            skLineSegment(sketch, "E51.11.5", {"start": v(27.07, 7.4) * mm, "end": v(27.75, 7.22) * mm});
            skLineSegment(sketch, "E51.11.6", {"start": v(26.5, 4.94) * mm, "end": v(26.98, 5.29) * mm});
            skLineSegment(sketch, "E51.11.7", {"start": v(28.55, 6.7) * mm, "end": v(29.11, 7.32) * mm});
            skLineSegment(sketch, "E51.11.8", {"start": v(26.07, 4.65) * mm, "end": v(26.5, 4.94) * mm});
            skLineSegment(sketch, "E51.11.9", {"start": v(28.48, 6.99) * mm, "end": v(29.26, 6.7) * mm});
            skLineSegment(sketch, "E51.11.10", {"start": v(28, 6.16) * mm, "end": v(28.55, 6.7) * mm});
            skLineSegment(sketch, "E51.11.11", {"start": v(25.86, 7.63) * mm, "end": v(26.44, 7.54) * mm});
            skLineSegment(sketch, "E51.11.12", {"start": v(27.75, 7.22) * mm, "end": v(28.48, 6.99) * mm});
            skLineSegment(sketch, "E51.11.13", {"start": v(25.02, 4.1) * mm, "end": v(25.32, 4.23) * mm});
            skLineSegment(sketch, "E51.11.14", {"start": v(25.32, 4.23) * mm, "end": v(25.68, 4.42) * mm});
            skLineSegment(sketch, "E51.11.15", {"start": v(25.68, 4.42) * mm, "end": v(26.07, 4.65) * mm});
            skLineSegment(sketch, "E51.11.16", {"start": v(24.88, 7.72) * mm, "end": v(25.34, 7.7) * mm});
            skLineSegment(sketch, "E51.11.17", {"start": v(24.48, 7.72) * mm, "end": v(24.88, 7.72) * mm});
            skLineSegment(sketch, "E51.11.18", {"start": v(25.34, 7.7) * mm, "end": v(25.86, 7.63) * mm});
            skLineSegment(sketch, "E51.11.19", {"start": v(24.76, 3.99) * mm, "end": v(25.02, 4.1) * mm});
            skLineSegment(sketch, "E51.11.20", {"start": v(24.56, 3.92) * mm, "end": v(24.76, 3.99) * mm});
            skLineSegment(sketch, "E51.11.21", {"start": v(24.15, 7.71) * mm, "end": v(24.48, 7.72) * mm});
            skLineSegment(sketch, "E51.11.22", {"start": v(23.87, 7.69) * mm, "end": v(24.15, 7.71) * mm});
            skLineSegment(sketch, "E51.11.23", {"start": v(23.5, 7.63) * mm, "end": v(23.66, 7.66) * mm});
            skLineSegment(sketch, "E51.11.24", {"start": v(24.29, 3.85) * mm, "end": v(24.32, 3.85) * mm});
            skLineSegment(sketch, "E51.11.25", {"start": v(24.32, 3.85) * mm, "end": v(24.4, 3.87) * mm});
            skLineSegment(sketch, "E51.11.26", {"start": v(23.66, 7.66) * mm, "end": v(23.87, 7.69) * mm});
            skLineSegment(sketch, "E51.11.27", {"start": v(24.4, 3.87) * mm, "end": v(24.56, 3.92) * mm});
            skLineSegment(sketch, "E51.11.28", {"start": v(23.42, 7.6) * mm, "end": v(23.5, 7.63) * mm});
            skLineSegment(sketch, "E51.11.29", {"start": v(23.39, 7.6) * mm, "end": v(23.42, 7.6) * mm});
            skLineSegment(sketch, "E52.2.12.0", {"start": v(18.17, 13.2) * mm, "end": v(19.9, 14.45) * mm});
            skLineSegment(sketch, "E52.3.12.0", {"start": v(24.38, 13.9) * mm, "end": v(24.73, 14.52) * mm});
            skLineSegment(sketch, "E52.6.12.0", {"start": v(20.01, 10.2) * mm, "end": v(21.91, 11.16) * mm});
            skLineSegment(sketch, "E52.9.12.0", {"start": v(24.03, 13.36) * mm, "end": v(24.38, 13.9) * mm});
            skLineSegment(sketch, "E52.12.12.0", {"start": v(22.82, 15.34) * mm, "end": v(23.46, 15.4) * mm});
            skLineSegment(sketch, "E52.15.12.0", {"start": v(23.46, 15.4) * mm, "end": v(24.16, 15.44) * mm});
            skLineSegment(sketch, "E52.18.12.0", {"start": v(23.69, 12.89) * mm, "end": v(24.03, 13.36) * mm});
            skLineSegment(sketch, "E52.21.12.0", {"start": v(25.08, 15.2) * mm, "end": v(25.42, 15.96) * mm});
            skLineSegment(sketch, "E52.24.12.0", {"start": v(23.36, 12.48) * mm, "end": v(23.69, 12.89) * mm});
            skLineSegment(sketch, "E52.27.12.0", {"start": v(24.93, 15.45) * mm, "end": v(25.76, 15.4) * mm});
            skLineSegment(sketch, "E52.30.12.0", {"start": v(24.73, 14.52) * mm, "end": v(25.08, 15.2) * mm});
            skLineSegment(sketch, "E52.33.12.0", {"start": v(22.24, 15.25) * mm, "end": v(22.82, 15.34) * mm});
            skLineSegment(sketch, "E52.36.12.0", {"start": v(24.16, 15.44) * mm, "end": v(24.93, 15.45) * mm});
            skLineSegment(sketch, "E52.39.12.0", {"start": v(22.53, 11.62) * mm, "end": v(22.78, 11.85) * mm});
            skLineSegment(sketch, "E52.42.12.0", {"start": v(22.78, 11.85) * mm, "end": v(23.05, 12.14) * mm});
            skLineSegment(sketch, "E52.45.12.0", {"start": v(23.05, 12.14) * mm, "end": v(23.36, 12.48) * mm});
            skLineSegment(sketch, "E52.48.12.0", {"start": v(21.28, 15.03) * mm, "end": v(21.73, 15.15) * mm});
            skLineSegment(sketch, "E52.51.12.0", {"start": v(20.9, 14.91) * mm, "end": v(21.28, 15.03) * mm});
            skLineSegment(sketch, "E52.54.12.0", {"start": v(21.73, 15.15) * mm, "end": v(22.24, 15.25) * mm});
            skLineSegment(sketch, "E52.57.12.0", {"start": v(22.31, 11.44) * mm, "end": v(22.53, 11.62) * mm});
            skLineSegment(sketch, "E52.60.12.0", {"start": v(22.14, 11.31) * mm, "end": v(22.31, 11.44) * mm});
            skLineSegment(sketch, "E52.63.12.0", {"start": v(20.58, 14.8) * mm, "end": v(20.9, 14.91) * mm});
            skLineSegment(sketch, "E52.66.12.0", {"start": v(20.33, 14.69) * mm, "end": v(20.58, 14.8) * mm});
            skLineSegment(sketch, "E52.69.12.0", {"start": v(20, 14.52) * mm, "end": v(20.13, 14.6) * mm});
            skLineSegment(sketch, "E52.72.12.0", {"start": v(21.91, 11.16) * mm, "end": v(21.94, 11.18) * mm});
            skLineSegment(sketch, "E52.75.12.0", {"start": v(21.94, 11.18) * mm, "end": v(22.02, 11.23) * mm});
            skLineSegment(sketch, "E52.78.12.0", {"start": v(20.13, 14.6) * mm, "end": v(20.33, 14.69) * mm});
            skLineSegment(sketch, "E52.81.12.0", {"start": v(22.02, 11.23) * mm, "end": v(22.14, 11.31) * mm});
            skLineSegment(sketch, "E52.84.12.0", {"start": v(19.92, 14.47) * mm, "end": v(20, 14.52) * mm});
            skLineSegment(sketch, "E52.87.12.0", {"start": v(19.9, 14.45) * mm, "end": v(19.92, 14.47) * mm});
            skLineSegment(sketch, "E52.2.13.0", {"start": v(13.2, 18.17) * mm, "end": v(14.45, 19.9) * mm});
            skLineSegment(sketch, "E52.3.13.0", {"start": v(18.89, 20.76) * mm, "end": v(19.03, 21.45) * mm});
            skLineSegment(sketch, "E52.6.13.0", {"start": v(15.88, 15.88) * mm, "end": v(17.39, 17.39) * mm});
            skLineSegment(sketch, "E52.9.13.0", {"start": v(18.72, 20.13) * mm, "end": v(18.89, 20.76) * mm});
            skLineSegment(sketch, "E52.12.13.0", {"start": v(16.96, 21.64) * mm, "end": v(17.55, 21.9) * mm});
            skLineSegment(sketch, "E52.15.13.0", {"start": v(17.55, 21.9) * mm, "end": v(18.2, 22.16) * mm});
            skLineSegment(sketch, "E52.18.13.0", {"start": v(18.54, 19.58) * mm, "end": v(18.72, 20.13) * mm});
            skLineSegment(sketch, "E52.21.13.0", {"start": v(19.16, 22.2) * mm, "end": v(19.25, 23.03) * mm});
            skLineSegment(sketch, "E52.24.13.0", {"start": v(18.36, 19.09) * mm, "end": v(18.54, 19.58) * mm});
            skLineSegment(sketch, "E52.27.13.0", {"start": v(18.94, 22.4) * mm, "end": v(19.74, 22.61) * mm});
            skLineSegment(sketch, "E52.30.13.0", {"start": v(19.03, 21.45) * mm, "end": v(19.16, 22.2) * mm});
            skLineSegment(sketch, "E52.33.13.0", {"start": v(16.44, 21.38) * mm, "end": v(16.96, 21.64) * mm});
            skLineSegment(sketch, "E52.36.13.0", {"start": v(18.2, 22.16) * mm, "end": v(18.94, 22.4) * mm});
            skLineSegment(sketch, "E52.39.13.0", {"start": v(17.83, 18.01) * mm, "end": v(18, 18.3) * mm});
            skLineSegment(sketch, "E52.42.13.0", {"start": v(18, 18.3) * mm, "end": v(18.18, 18.67) * mm});
            skLineSegment(sketch, "E52.45.13.0", {"start": v(18.18, 18.67) * mm, "end": v(18.36, 19.09) * mm});
            skLineSegment(sketch, "E52.48.13.0", {"start": v(15.6, 20.87) * mm, "end": v(15.98, 21.12) * mm});
            skLineSegment(sketch, "E52.51.13.0", {"start": v(15.27, 20.64) * mm, "end": v(15.6, 20.87) * mm});
            skLineSegment(sketch, "E52.54.13.0", {"start": v(15.98, 21.12) * mm, "end": v(16.44, 21.38) * mm});
            skLineSegment(sketch, "E52.57.13.0", {"start": v(17.69, 17.78) * mm, "end": v(17.83, 18.01) * mm});
            skLineSegment(sketch, "E52.60.13.0", {"start": v(17.56, 17.6) * mm, "end": v(17.69, 17.78) * mm});
            skLineSegment(sketch, "E52.63.13.0", {"start": v(15, 20.43) * mm, "end": v(15.27, 20.64) * mm});
            skLineSegment(sketch, "E52.66.13.0", {"start": v(14.8, 20.25) * mm, "end": v(15, 20.43) * mm});
            skLineSegment(sketch, "E52.69.13.0", {"start": v(14.53, 19.99) * mm, "end": v(14.64, 20.1) * mm});
            skLineSegment(sketch, "E52.72.13.0", {"start": v(17.39, 17.39) * mm, "end": v(17.4, 17.41) * mm});
            skLineSegment(sketch, "E52.75.13.0", {"start": v(17.4, 17.41) * mm, "end": v(17.47, 17.48) * mm});
            skLineSegment(sketch, "E52.78.13.0", {"start": v(14.64, 20.1) * mm, "end": v(14.8, 20.25) * mm});
            skLineSegment(sketch, "E52.81.13.0", {"start": v(17.47, 17.48) * mm, "end": v(17.56, 17.6) * mm});
            skLineSegment(sketch, "E52.84.13.0", {"start": v(14.47, 19.92) * mm, "end": v(14.53, 19.99) * mm});
            skLineSegment(sketch, "E52.87.13.0", {"start": v(14.45, 19.9) * mm, "end": v(14.47, 19.92) * mm});
            skLineSegment(sketch, "E52.2.14.0", {"start": v(6.94, 21.36) * mm, "end": v(7.6, 23.39) * mm});
            skLineSegment(sketch, "E52.3.14.0", {"start": v(11.55, 25.58) * mm, "end": v(11.47, 26.28) * mm});
            skLineSegment(sketch, "E52.6.14.0", {"start": v(10.2, 20.01) * mm, "end": v(11.16, 21.91) * mm});
            skLineSegment(sketch, "E52.9.14.0", {"start": v(11.58, 24.93) * mm, "end": v(11.55, 25.58) * mm});
            skLineSegment(sketch, "E52.12.14.0", {"start": v(9.44, 25.82) * mm, "end": v(9.92, 26.25) * mm});
            skLineSegment(sketch, "E52.15.14.0", {"start": v(9.92, 26.25) * mm, "end": v(10.47, 26.7) * mm});
            skLineSegment(sketch, "E52.18.14.0", {"start": v(11.59, 24.35) * mm, "end": v(11.58, 24.93) * mm});
            skLineSegment(sketch, "E52.21.14.0", {"start": v(11.36, 27.04) * mm, "end": v(11.19, 27.85) * mm});
            skLineSegment(sketch, "E52.24.14.0", {"start": v(11.56, 23.83) * mm, "end": v(11.59, 24.35) * mm});
            skLineSegment(sketch, "E52.27.14.0", {"start": v(11.1, 27.15) * mm, "end": v(11.78, 27.6) * mm});
            skLineSegment(sketch, "E52.30.14.0", {"start": v(11.47, 26.28) * mm, "end": v(11.36, 27.04) * mm});
            skLineSegment(sketch, "E52.33.14.0", {"start": v(9.03, 25.41) * mm, "end": v(9.44, 25.82) * mm});
            skLineSegment(sketch, "E52.36.14.0", {"start": v(10.47, 26.7) * mm, "end": v(11.1, 27.15) * mm});
            skLineSegment(sketch, "E52.39.14.0", {"start": v(11.4, 22.64) * mm, "end": v(11.46, 22.97) * mm});
            skLineSegment(sketch, "E52.42.14.0", {"start": v(11.46, 22.97) * mm, "end": v(11.52, 23.37) * mm});
            skLineSegment(sketch, "E52.45.14.0", {"start": v(11.52, 23.37) * mm, "end": v(11.56, 23.83) * mm});
            skLineSegment(sketch, "E52.48.14.0", {"start": v(8.38, 24.67) * mm, "end": v(8.67, 25.02) * mm});
            skLineSegment(sketch, "E52.51.14.0", {"start": v(8.14, 24.35) * mm, "end": v(8.38, 24.67) * mm});
            skLineSegment(sketch, "E52.54.14.0", {"start": v(8.67, 25.02) * mm, "end": v(9.03, 25.41) * mm});
            skLineSegment(sketch, "E52.57.14.0", {"start": v(11.33, 22.37) * mm, "end": v(11.4, 22.64) * mm});
            skLineSegment(sketch, "E52.60.14.0", {"start": v(11.26, 22.17) * mm, "end": v(11.33, 22.37) * mm});
            skLineSegment(sketch, "E52.63.14.0", {"start": v(7.95, 24.07) * mm, "end": v(8.14, 24.35) * mm});
            skLineSegment(sketch, "E52.66.14.0", {"start": v(7.81, 23.83) * mm, "end": v(7.95, 24.07) * mm});
            skLineSegment(sketch, "E52.69.14.0", {"start": v(7.64, 23.5) * mm, "end": v(7.71, 23.64) * mm});
            skLineSegment(sketch, "E52.72.14.0", {"start": v(11.16, 21.91) * mm, "end": v(11.18, 21.94) * mm});
            skLineSegment(sketch, "E52.75.14.0", {"start": v(11.18, 21.94) * mm, "end": v(11.21, 22.02) * mm});
            skLineSegment(sketch, "E52.78.14.0", {"start": v(7.71, 23.64) * mm, "end": v(7.81, 23.83) * mm});
            skLineSegment(sketch, "E52.81.14.0", {"start": v(11.21, 22.02) * mm, "end": v(11.26, 22.17) * mm});
            skLineSegment(sketch, "E52.84.14.0", {"start": v(7.6, 23.42) * mm, "end": v(7.64, 23.5) * mm});
            skLineSegment(sketch, "E52.87.14.0", {"start": v(7.6, 23.39) * mm, "end": v(7.6, 23.42) * mm});
            skLineSegment(sketch, "E52.2.15.0", {"start": v(0, 22.46) * mm, "end": v(0, 24.6) * mm});
            skLineSegment(sketch, "E52.3.15.0", {"start": v(3.08, 27.9) * mm, "end": v(2.8, 28.54) * mm});
            skLineSegment(sketch, "E52.6.15.0", {"start": v(3.51, 22.18) * mm, "end": v(3.85, 24.29) * mm});
            skLineSegment(sketch, "E52.9.15.0", {"start": v(3.31, 27.3) * mm, "end": v(3.08, 27.9) * mm});
            skLineSegment(sketch, "E52.12.15.0", {"start": v(1, 27.48) * mm, "end": v(1.32, 28.03) * mm});
            skLineSegment(sketch, "E52.15.15.0", {"start": v(1.32, 28.03) * mm, "end": v(1.7, 28.63) * mm});
            skLineSegment(sketch, "E52.18.15.0", {"start": v(3.5, 26.74) * mm, "end": v(3.31, 27.3) * mm});
            skLineSegment(sketch, "E52.21.15.0", {"start": v(2.44, 29.23) * mm, "end": v(2.03, 29.95) * mm});
            skLineSegment(sketch, "E52.24.15.0", {"start": v(3.63, 26.23) * mm, "end": v(3.5, 26.74) * mm});
            skLineSegment(sketch, "E52.27.15.0", {"start": v(2.16, 29.25) * mm, "end": v(2.68, 29.9) * mm});
            skLineSegment(sketch, "E52.30.15.0", {"start": v(2.8, 28.54) * mm, "end": v(2.44, 29.23) * mm});
            skLineSegment(sketch, "E52.33.15.0", {"start": v(0.73, 26.96) * mm, "end": v(1, 27.48) * mm});
            skLineSegment(sketch, "E52.36.15.0", {"start": v(1.7, 28.63) * mm, "end": v(2.16, 29.25) * mm});
            skLineSegment(sketch, "E52.39.15.0", {"start": v(3.84, 25.06) * mm, "end": v(3.8, 25.4) * mm});
            skLineSegment(sketch, "E52.42.15.0", {"start": v(3.8, 25.4) * mm, "end": v(3.73, 25.78) * mm});
            skLineSegment(sketch, "E52.45.15.0", {"start": v(3.73, 25.78) * mm, "end": v(3.63, 26.23) * mm});
            skLineSegment(sketch, "E52.48.15.0", {"start": v(0.35, 26.05) * mm, "end": v(0.52, 26.48) * mm});
            skLineSegment(sketch, "E52.51.15.0", {"start": v(0.22, 25.67) * mm, "end": v(0.35, 26.05) * mm});
            skLineSegment(sketch, "E52.54.15.0", {"start": v(0.52, 26.48) * mm, "end": v(0.73, 26.96) * mm});
            skLineSegment(sketch, "E52.57.15.0", {"start": v(3.86, 24.78) * mm, "end": v(3.84, 25.06) * mm});
            skLineSegment(sketch, "E52.60.15.0", {"start": v(3.86, 24.56) * mm, "end": v(3.86, 24.78) * mm});
            skLineSegment(sketch, "E52.63.15.0", {"start": v(0.13, 25.35) * mm, "end": v(0.22, 25.67) * mm});
            skLineSegment(sketch, "E52.66.15.0", {"start": v(0.07, 25.08) * mm, "end": v(0.13, 25.35) * mm});
            skLineSegment(sketch, "E52.69.15.0", {"start": v(0, 24.71) * mm, "end": v(0.03, 24.87) * mm});
            skLineSegment(sketch, "E52.72.15.0", {"start": v(3.85, 24.29) * mm, "end": v(3.85, 24.32) * mm});
            skLineSegment(sketch, "E52.75.15.0", {"start": v(3.85, 24.32) * mm, "end": v(3.86, 24.41) * mm});
            skLineSegment(sketch, "E52.78.15.0", {"start": v(0.03, 24.87) * mm, "end": v(0.07, 25.08) * mm});
            skLineSegment(sketch, "E52.81.15.0", {"start": v(3.86, 24.41) * mm, "end": v(3.86, 24.56) * mm});
            skLineSegment(sketch, "E52.84.15.0", {"start": v(0, 24.62) * mm, "end": v(0, 24.71) * mm});
            skLineSegment(sketch, "E52.87.15.0", {"start": v(0, 24.6) * mm, "end": v(0, 24.62) * mm});
            skLineSegment(sketch, "E52.2.16.0", {"start": v(-6.94, 21.36) * mm, "end": v(-7.6, 23.39) * mm});
            skLineSegment(sketch, "E52.3.16.0", {"start": v(-5.7, 27.48) * mm, "end": v(-6.16, 28) * mm});
            skLineSegment(sketch, "E52.6.16.0", {"start": v(-3.51, 22.18) * mm, "end": v(-3.85, 24.29) * mm});
            skLineSegment(sketch, "E52.9.16.0", {"start": v(-5.29, 26.98) * mm, "end": v(-5.7, 27.48) * mm});
            skLineSegment(sketch, "E52.12.16.0", {"start": v(-7.54, 26.44) * mm, "end": v(-7.4, 27.07) * mm});
            skLineSegment(sketch, "E52.15.16.0", {"start": v(-7.4, 27.07) * mm, "end": v(-7.22, 27.75) * mm});
            skLineSegment(sketch, "E52.18.16.0", {"start": v(-4.94, 26.5) * mm, "end": v(-5.29, 26.98) * mm});
            skLineSegment(sketch, "E52.21.16.0", {"start": v(-6.7, 28.55) * mm, "end": v(-7.32, 29.11) * mm});
            skLineSegment(sketch, "E52.24.16.0", {"start": v(-4.65, 26.07) * mm, "end": v(-4.94, 26.5) * mm});
            skLineSegment(sketch, "E52.27.16.0", {"start": v(-6.99, 28.48) * mm, "end": v(-6.7, 29.26) * mm});
            skLineSegment(sketch, "E52.30.16.0", {"start": v(-6.16, 28) * mm, "end": v(-6.7, 28.55) * mm});
            skLineSegment(sketch, "E52.33.16.0", {"start": v(-7.63, 25.86) * mm, "end": v(-7.54, 26.44) * mm});
            skLineSegment(sketch, "E52.36.16.0", {"start": v(-7.22, 27.75) * mm, "end": v(-6.99, 28.48) * mm});
            skLineSegment(sketch, "E52.39.16.0", {"start": v(-4.1, 25.02) * mm, "end": v(-4.23, 25.32) * mm});
            skLineSegment(sketch, "E52.42.16.0", {"start": v(-4.23, 25.32) * mm, "end": v(-4.42, 25.68) * mm});
            skLineSegment(sketch, "E52.45.16.0", {"start": v(-4.42, 25.68) * mm, "end": v(-4.65, 26.07) * mm});
            skLineSegment(sketch, "E52.48.16.0", {"start": v(-7.72, 24.88) * mm, "end": v(-7.7, 25.34) * mm});
            skLineSegment(sketch, "E52.51.16.0", {"start": v(-7.72, 24.48) * mm, "end": v(-7.72, 24.88) * mm});
            skLineSegment(sketch, "E52.54.16.0", {"start": v(-7.7, 25.34) * mm, "end": v(-7.63, 25.86) * mm});
            skLineSegment(sketch, "E52.57.16.0", {"start": v(-3.99, 24.76) * mm, "end": v(-4.1, 25.02) * mm});
            skLineSegment(sketch, "E52.60.16.0", {"start": v(-3.92, 24.56) * mm, "end": v(-3.99, 24.76) * mm});
            skLineSegment(sketch, "E52.63.16.0", {"start": v(-7.71, 24.15) * mm, "end": v(-7.72, 24.48) * mm});
            skLineSegment(sketch, "E52.66.16.0", {"start": v(-7.69, 23.87) * mm, "end": v(-7.71, 24.15) * mm});
            skLineSegment(sketch, "E52.69.16.0", {"start": v(-7.63, 23.5) * mm, "end": v(-7.66, 23.66) * mm});
            skLineSegment(sketch, "E52.72.16.0", {"start": v(-3.85, 24.29) * mm, "end": v(-3.85, 24.32) * mm});
            skLineSegment(sketch, "E52.75.16.0", {"start": v(-3.85, 24.32) * mm, "end": v(-3.87, 24.4) * mm});
            skLineSegment(sketch, "E52.78.16.0", {"start": v(-7.66, 23.66) * mm, "end": v(-7.69, 23.87) * mm});
            skLineSegment(sketch, "E52.81.16.0", {"start": v(-3.87, 24.4) * mm, "end": v(-3.92, 24.56) * mm});
            skLineSegment(sketch, "E52.84.16.0", {"start": v(-7.6, 23.42) * mm, "end": v(-7.63, 23.5) * mm});
            skLineSegment(sketch, "E52.87.16.0", {"start": v(-7.6, 23.39) * mm, "end": v(-7.6, 23.42) * mm});
            skLineSegment(sketch, "E52.2.17.0", {"start": v(-13.2, 18.17) * mm, "end": v(-14.45, 19.9) * mm});
            skLineSegment(sketch, "E52.3.17.0", {"start": v(-13.9, 24.38) * mm, "end": v(-14.52, 24.73) * mm});
            skLineSegment(sketch, "E52.6.17.0", {"start": v(-10.2, 20.01) * mm, "end": v(-11.16, 21.91) * mm});
            skLineSegment(sketch, "E52.9.17.0", {"start": v(-13.36, 24.03) * mm, "end": v(-13.9, 24.38) * mm});
            skLineSegment(sketch, "E52.12.17.0", {"start": v(-15.34, 22.82) * mm, "end": v(-15.4, 23.46) * mm});
            skLineSegment(sketch, "E52.15.17.0", {"start": v(-15.4, 23.46) * mm, "end": v(-15.44, 24.16) * mm});
            skLineSegment(sketch, "E52.18.17.0", {"start": v(-12.89, 23.69) * mm, "end": v(-13.36, 24.03) * mm});
            skLineSegment(sketch, "E52.21.17.0", {"start": v(-15.2, 25.08) * mm, "end": v(-15.96, 25.42) * mm});
            skLineSegment(sketch, "E52.24.17.0", {"start": v(-12.48, 23.36) * mm, "end": v(-12.89, 23.69) * mm});
            skLineSegment(sketch, "E52.27.17.0", {"start": v(-15.45, 24.93) * mm, "end": v(-15.4, 25.76) * mm});
            skLineSegment(sketch, "E52.30.17.0", {"start": v(-14.52, 24.73) * mm, "end": v(-15.2, 25.08) * mm});
            skLineSegment(sketch, "E52.33.17.0", {"start": v(-15.25, 22.24) * mm, "end": v(-15.34, 22.82) * mm});
            skLineSegment(sketch, "E52.36.17.0", {"start": v(-15.44, 24.16) * mm, "end": v(-15.45, 24.93) * mm});
            skLineSegment(sketch, "E52.39.17.0", {"start": v(-11.62, 22.53) * mm, "end": v(-11.85, 22.78) * mm});
            skLineSegment(sketch, "E52.42.17.0", {"start": v(-11.85, 22.78) * mm, "end": v(-12.14, 23.05) * mm});
            skLineSegment(sketch, "E52.45.17.0", {"start": v(-12.14, 23.05) * mm, "end": v(-12.48, 23.36) * mm});
            skLineSegment(sketch, "E52.48.17.0", {"start": v(-15.03, 21.28) * mm, "end": v(-15.15, 21.73) * mm});
            skLineSegment(sketch, "E52.51.17.0", {"start": v(-14.91, 20.9) * mm, "end": v(-15.03, 21.28) * mm});
            skLineSegment(sketch, "E52.54.17.0", {"start": v(-15.15, 21.73) * mm, "end": v(-15.25, 22.24) * mm});
            skLineSegment(sketch, "E52.57.17.0", {"start": v(-11.44, 22.31) * mm, "end": v(-11.62, 22.53) * mm});
            skLineSegment(sketch, "E52.60.17.0", {"start": v(-11.31, 22.14) * mm, "end": v(-11.44, 22.31) * mm});
            skLineSegment(sketch, "E52.63.17.0", {"start": v(-14.8, 20.58) * mm, "end": v(-14.91, 20.9) * mm});
            skLineSegment(sketch, "E52.66.17.0", {"start": v(-14.69, 20.33) * mm, "end": v(-14.8, 20.58) * mm});
            skLineSegment(sketch, "E52.69.17.0", {"start": v(-14.52, 20) * mm, "end": v(-14.6, 20.13) * mm});
            skLineSegment(sketch, "E52.72.17.0", {"start": v(-11.16, 21.91) * mm, "end": v(-11.18, 21.94) * mm});
            skLineSegment(sketch, "E52.75.17.0", {"start": v(-11.18, 21.94) * mm, "end": v(-11.23, 22.02) * mm});
            skLineSegment(sketch, "E52.78.17.0", {"start": v(-14.6, 20.13) * mm, "end": v(-14.69, 20.33) * mm});
            skLineSegment(sketch, "E52.81.17.0", {"start": v(-11.23, 22.02) * mm, "end": v(-11.31, 22.14) * mm});
            skLineSegment(sketch, "E52.84.17.0", {"start": v(-14.47, 19.92) * mm, "end": v(-14.52, 20) * mm});
            skLineSegment(sketch, "E52.87.17.0", {"start": v(-14.45, 19.9) * mm, "end": v(-14.47, 19.92) * mm});
            skLineSegment(sketch, "E52.2.18.0", {"start": v(-18.17, 13.2) * mm, "end": v(-19.9, 14.45) * mm});
            skLineSegment(sketch, "E52.3.18.0", {"start": v(-20.76, 18.89) * mm, "end": v(-21.45, 19.03) * mm});
            skLineSegment(sketch, "E52.6.18.0", {"start": v(-15.88, 15.88) * mm, "end": v(-17.39, 17.39) * mm});
            skLineSegment(sketch, "E52.9.18.0", {"start": v(-20.13, 18.72) * mm, "end": v(-20.76, 18.89) * mm});
            skLineSegment(sketch, "E52.12.18.0", {"start": v(-21.64, 16.96) * mm, "end": v(-21.9, 17.55) * mm});
            skLineSegment(sketch, "E52.15.18.0", {"start": v(-21.9, 17.55) * mm, "end": v(-22.16, 18.2) * mm});
            skLineSegment(sketch, "E52.18.18.0", {"start": v(-19.58, 18.54) * mm, "end": v(-20.13, 18.72) * mm});
            skLineSegment(sketch, "E52.21.18.0", {"start": v(-22.2, 19.16) * mm, "end": v(-23.03, 19.25) * mm});
            skLineSegment(sketch, "E52.24.18.0", {"start": v(-19.09, 18.36) * mm, "end": v(-19.58, 18.54) * mm});
            skLineSegment(sketch, "E52.27.18.0", {"start": v(-22.4, 18.94) * mm, "end": v(-22.61, 19.74) * mm});
            skLineSegment(sketch, "E52.30.18.0", {"start": v(-21.45, 19.03) * mm, "end": v(-22.2, 19.16) * mm});
            skLineSegment(sketch, "E52.33.18.0", {"start": v(-21.38, 16.44) * mm, "end": v(-21.64, 16.96) * mm});
            skLineSegment(sketch, "E52.36.18.0", {"start": v(-22.16, 18.2) * mm, "end": v(-22.4, 18.94) * mm});
            skLineSegment(sketch, "E52.39.18.0", {"start": v(-18.01, 17.83) * mm, "end": v(-18.3, 18) * mm});
            skLineSegment(sketch, "E52.42.18.0", {"start": v(-18.3, 18) * mm, "end": v(-18.67, 18.18) * mm});
            skLineSegment(sketch, "E52.45.18.0", {"start": v(-18.67, 18.18) * mm, "end": v(-19.09, 18.36) * mm});
            skLineSegment(sketch, "E52.48.18.0", {"start": v(-20.87, 15.6) * mm, "end": v(-21.12, 15.98) * mm});
            skLineSegment(sketch, "E52.51.18.0", {"start": v(-20.64, 15.27) * mm, "end": v(-20.87, 15.6) * mm});
            skLineSegment(sketch, "E52.54.18.0", {"start": v(-21.12, 15.98) * mm, "end": v(-21.38, 16.44) * mm});
            skLineSegment(sketch, "E52.57.18.0", {"start": v(-17.78, 17.69) * mm, "end": v(-18.01, 17.83) * mm});
            skLineSegment(sketch, "E52.60.18.0", {"start": v(-17.6, 17.56) * mm, "end": v(-17.78, 17.69) * mm});
            skLineSegment(sketch, "E52.63.18.0", {"start": v(-20.43, 15) * mm, "end": v(-20.64, 15.27) * mm});
            skLineSegment(sketch, "E52.66.18.0", {"start": v(-20.25, 14.8) * mm, "end": v(-20.43, 15) * mm});
            skLineSegment(sketch, "E52.69.18.0", {"start": v(-19.99, 14.53) * mm, "end": v(-20.1, 14.64) * mm});
            skLineSegment(sketch, "E52.72.18.0", {"start": v(-17.39, 17.39) * mm, "end": v(-17.41, 17.4) * mm});
            skLineSegment(sketch, "E52.75.18.0", {"start": v(-17.41, 17.4) * mm, "end": v(-17.48, 17.47) * mm});
            skLineSegment(sketch, "E52.78.18.0", {"start": v(-20.1, 14.64) * mm, "end": v(-20.25, 14.8) * mm});
            skLineSegment(sketch, "E52.81.18.0", {"start": v(-17.48, 17.47) * mm, "end": v(-17.6, 17.56) * mm});
            skLineSegment(sketch, "E52.84.18.0", {"start": v(-19.92, 14.47) * mm, "end": v(-19.99, 14.53) * mm});
            skLineSegment(sketch, "E52.87.18.0", {"start": v(-19.9, 14.45) * mm, "end": v(-19.92, 14.47) * mm});
            skLineSegment(sketch, "E52.2.19.0", {"start": v(-21.36, 6.94) * mm, "end": v(-23.39, 7.6) * mm});
            skLineSegment(sketch, "E52.3.19.0", {"start": v(-25.58, 11.55) * mm, "end": v(-26.28, 11.47) * mm});
            skLineSegment(sketch, "E52.6.19.0", {"start": v(-20.01, 10.2) * mm, "end": v(-21.91, 11.16) * mm});
            skLineSegment(sketch, "E52.9.19.0", {"start": v(-24.93, 11.58) * mm, "end": v(-25.58, 11.55) * mm});
            skLineSegment(sketch, "E52.12.19.0", {"start": v(-25.82, 9.44) * mm, "end": v(-26.25, 9.92) * mm});
            skLineSegment(sketch, "E52.15.19.0", {"start": v(-26.25, 9.92) * mm, "end": v(-26.7, 10.47) * mm});
            skLineSegment(sketch, "E52.18.19.0", {"start": v(-24.35, 11.59) * mm, "end": v(-24.93, 11.58) * mm});
            skLineSegment(sketch, "E52.21.19.0", {"start": v(-27.04, 11.36) * mm, "end": v(-27.85, 11.19) * mm});
            skLineSegment(sketch, "E52.24.19.0", {"start": v(-23.83, 11.56) * mm, "end": v(-24.35, 11.59) * mm});
            skLineSegment(sketch, "E52.27.19.0", {"start": v(-27.15, 11.1) * mm, "end": v(-27.6, 11.78) * mm});
            skLineSegment(sketch, "E52.30.19.0", {"start": v(-26.28, 11.47) * mm, "end": v(-27.04, 11.36) * mm});
            skLineSegment(sketch, "E52.33.19.0", {"start": v(-25.41, 9.03) * mm, "end": v(-25.82, 9.44) * mm});
            skLineSegment(sketch, "E52.36.19.0", {"start": v(-26.7, 10.47) * mm, "end": v(-27.15, 11.1) * mm});
            skLineSegment(sketch, "E52.39.19.0", {"start": v(-22.64, 11.4) * mm, "end": v(-22.97, 11.46) * mm});
            skLineSegment(sketch, "E52.42.19.0", {"start": v(-22.97, 11.46) * mm, "end": v(-23.37, 11.52) * mm});
            skLineSegment(sketch, "E52.45.19.0", {"start": v(-23.37, 11.52) * mm, "end": v(-23.83, 11.56) * mm});
            skLineSegment(sketch, "E52.48.19.0", {"start": v(-24.67, 8.38) * mm, "end": v(-25.02, 8.67) * mm});
            skLineSegment(sketch, "E52.51.19.0", {"start": v(-24.35, 8.14) * mm, "end": v(-24.67, 8.38) * mm});
            skLineSegment(sketch, "E52.54.19.0", {"start": v(-25.02, 8.67) * mm, "end": v(-25.41, 9.03) * mm});
            skLineSegment(sketch, "E52.57.19.0", {"start": v(-22.37, 11.33) * mm, "end": v(-22.64, 11.4) * mm});
            skLineSegment(sketch, "E52.60.19.0", {"start": v(-22.17, 11.26) * mm, "end": v(-22.37, 11.33) * mm});
            skLineSegment(sketch, "E52.63.19.0", {"start": v(-24.07, 7.95) * mm, "end": v(-24.35, 8.14) * mm});
            skLineSegment(sketch, "E52.66.19.0", {"start": v(-23.83, 7.81) * mm, "end": v(-24.07, 7.95) * mm});
            skLineSegment(sketch, "E52.69.19.0", {"start": v(-23.5, 7.64) * mm, "end": v(-23.64, 7.71) * mm});
            skLineSegment(sketch, "E52.72.19.0", {"start": v(-21.91, 11.16) * mm, "end": v(-21.94, 11.18) * mm});
            skLineSegment(sketch, "E52.75.19.0", {"start": v(-21.94, 11.18) * mm, "end": v(-22.02, 11.21) * mm});
            skLineSegment(sketch, "E52.78.19.0", {"start": v(-23.64, 7.71) * mm, "end": v(-23.83, 7.81) * mm});
            skLineSegment(sketch, "E52.81.19.0", {"start": v(-22.02, 11.21) * mm, "end": v(-22.17, 11.26) * mm});
            skLineSegment(sketch, "E52.84.19.0", {"start": v(-23.42, 7.6) * mm, "end": v(-23.5, 7.64) * mm});
            skLineSegment(sketch, "E52.87.19.0", {"start": v(-23.39, 7.6) * mm, "end": v(-23.42, 7.6) * mm});
            skSolve(sketch);
        }
        {
            var Q0;
            {var subQ0=sQuery(id+"F1.wireOp",EDGE,"E0");var subQ27=makeQuery(id+"F1.imprint","INTERSECT",VERTEX,{"derivedFrom":[subQ0,sQuery(id+"F1.wireOp",EDGE,"E51.10.0")]});Q0=makeQuery(id+"F1.imprint","IMPRINT",FACE,{"disambiguationData":[TD([[makeQuery(id+"F1.imprint","IMPRINT",EDGE,{"disambiguationData":[TD([[subQ27,-1.0]])],"derivedFrom":subQ0}),1.0]])]});}
            var Q1;
            {var subQ0=sQuery(id+"F1.wireOp",EDGE,"E51.1.0");Q1=makeQuery(id+"F1.imprint","IMPRINT",FACE,{"disambiguationData":[TD([[makeQuery(id+"F1.imprint","IMPRINT",EDGE,{"derivedFrom":subQ0}),-1.0]])]});}
            var Q2;
            {var subQ7=sQuery(id+"F1.wireOp",EDGE,"E51.2.0");Q2=makeQuery(id+"F1.imprint","IMPRINT",FACE,{"disambiguationData":[TD([[makeQuery(id+"F1.imprint","IMPRINT",EDGE,{"derivedFrom":subQ7}),-1.0]])]});}
            var Q3;
            {var subQ8=sQuery(id+"F1.wireOp",EDGE,"E51.3.0");Q3=makeQuery(id+"F1.imprint","IMPRINT",FACE,{"disambiguationData":[TD([[makeQuery(id+"F1.imprint","IMPRINT",EDGE,{"derivedFrom":subQ8}),-1.0]])]});}
            var Q4;
            {var subQ2=sQuery(id+"F1.wireOp",EDGE,"E51.4.0");Q4=makeQuery(id+"F1.imprint","IMPRINT",FACE,{"disambiguationData":[TD([[makeQuery(id+"F1.imprint","IMPRINT",EDGE,{"derivedFrom":subQ2}),-1.0]])]});}
            var Q5;
            {var subQ8=sQuery(id+"F1.wireOp",EDGE,"E51.5.0");Q5=makeQuery(id+"F1.imprint","IMPRINT",FACE,{"disambiguationData":[TD([[makeQuery(id+"F1.imprint","IMPRINT",EDGE,{"derivedFrom":subQ8}),-1.0]])]});}
            var Q6;
            {var subQ3=sQuery(id+"F1.wireOp",EDGE,"E51.6.0");Q6=makeQuery(id+"F1.imprint","IMPRINT",FACE,{"disambiguationData":[TD([[makeQuery(id+"F1.imprint","IMPRINT",EDGE,{"derivedFrom":subQ3}),-1.0]])]});}
            var Q7;
            {var subQ0=sQuery(id+"F1.wireOp",EDGE,"E51.7.0");Q7=makeQuery(id+"F1.imprint","IMPRINT",FACE,{"disambiguationData":[TD([[makeQuery(id+"F1.imprint","IMPRINT",EDGE,{"derivedFrom":subQ0}),-1.0]])]});}
            var Q8;
            {var subQ5=sQuery(id+"F1.wireOp",EDGE,"E51.8.0");Q8=makeQuery(id+"F1.imprint","IMPRINT",FACE,{"disambiguationData":[TD([[makeQuery(id+"F1.imprint","IMPRINT",EDGE,{"derivedFrom":subQ5}),-1.0]])]});}
            var Q9;
            {var subQ1=sQuery(id+"F1.wireOp",EDGE,"E51.9.0");Q9=makeQuery(id+"F1.imprint","IMPRINT",FACE,{"disambiguationData":[TD([[makeQuery(id+"F1.imprint","IMPRINT",EDGE,{"derivedFrom":subQ1}),-1.0]])]});}
            var Q10;
            {var subQ5=sQuery(id+"F1.wireOp",EDGE,"E51.10.0");Q10=makeQuery(id+"F1.imprint","IMPRINT",FACE,{"disambiguationData":[TD([[makeQuery(id+"F1.imprint","IMPRINT",EDGE,{"derivedFrom":subQ5}),-1.0]])]});}
            var Q11;
            {var subQ8=sQuery(id+"F1.wireOp",EDGE,"E51.11.0");Q11=makeQuery(id+"F1.imprint","IMPRINT",FACE,{"disambiguationData":[TD([[makeQuery(id+"F1.imprint","IMPRINT",EDGE,{"derivedFrom":subQ8}),-1.0]])]});}
            var Q12;
            {var subQ2=sQuery(id+"F1.wireOp",EDGE,"E51.12.0");Q12=makeQuery(id+"F1.imprint","IMPRINT",FACE,{"disambiguationData":[TD([[makeQuery(id+"F1.imprint","IMPRINT",EDGE,{"derivedFrom":subQ2}),-1.0]])]});}
            var Q13;
            {var subQ3=sQuery(id+"F1.wireOp",EDGE,"E51.13.0");Q13=makeQuery(id+"F1.imprint","IMPRINT",FACE,{"disambiguationData":[TD([[makeQuery(id+"F1.imprint","IMPRINT",EDGE,{"derivedFrom":subQ3}),-1.0]])]});}
            var Q14;
            {var subQ0=sQuery(id+"F1.wireOp",EDGE,"E51.14.0");Q14=makeQuery(id+"F1.imprint","IMPRINT",FACE,{"disambiguationData":[TD([[makeQuery(id+"F1.imprint","IMPRINT",EDGE,{"derivedFrom":subQ0}),-1.0]])]});}
            var Q15;
            {var subQ6=sQuery(id+"F1.wireOp",EDGE,"E51.15.0");Q15=makeQuery(id+"F1.imprint","IMPRINT",FACE,{"disambiguationData":[TD([[makeQuery(id+"F1.imprint","IMPRINT",EDGE,{"derivedFrom":subQ6}),-1.0]])]});}
            var Q16;
            {var subQ5=sQuery(id+"F1.wireOp",EDGE,"E51.16.0");Q16=makeQuery(id+"F1.imprint","IMPRINT",FACE,{"disambiguationData":[TD([[makeQuery(id+"F1.imprint","IMPRINT",EDGE,{"derivedFrom":subQ5}),-1.0]])]});}
            var Q17;
            {var subQ7=sQuery(id+"F1.wireOp",EDGE,"E51.17.0");Q17=makeQuery(id+"F1.imprint","IMPRINT",FACE,{"disambiguationData":[TD([[makeQuery(id+"F1.imprint","IMPRINT",EDGE,{"derivedFrom":subQ7}),-1.0]])]});}
            var Q18;
            {var subQ5=sQuery(id+"F1.wireOp",EDGE,"E51.18.0");Q18=makeQuery(id+"F1.imprint","IMPRINT",FACE,{"disambiguationData":[TD([[makeQuery(id+"F1.imprint","IMPRINT",EDGE,{"derivedFrom":subQ5}),-1.0]])]});}
            var Q19;
            {var subQ8=sQuery(id+"F1.wireOp",EDGE,"E51.19.0");Q19=makeQuery(id+"F1.imprint","IMPRINT",FACE,{"disambiguationData":[TD([[makeQuery(id+"F1.imprint","IMPRINT",EDGE,{"derivedFrom":subQ8}),-1.0]])]});}
            var Q20;
            {var subQ8=sQuery(id+"F1.wireOp",EDGE,"E21");Q20=makeQuery(id+"F1.imprint","IMPRINT",FACE,{"disambiguationData":[TD([[makeQuery(id+"F1.imprint","IMPRINT",EDGE,{"derivedFrom":subQ8}),-1.0]])]});}
            var Q21;
            {var subQ2=sQuery(id+"F1.wireOp",EDGE,"E52.2.12.0");Q21=makeQuery(id+"F1.imprint","IMPRINT",FACE,{"disambiguationData":[TD([[makeQuery(id+"F1.imprint","IMPRINT",EDGE,{"derivedFrom":subQ2}),-1.0]])]});}
            var Q22;
            {var subQ7=sQuery(id+"F1.wireOp",EDGE,"E52.2.13.0");Q22=makeQuery(id+"F1.imprint","IMPRINT",FACE,{"disambiguationData":[TD([[makeQuery(id+"F1.imprint","IMPRINT",EDGE,{"derivedFrom":subQ7}),-1.0]])]});}
            var Q23;
            {var subQ7=sQuery(id+"F1.wireOp",EDGE,"E52.2.14.0");Q23=makeQuery(id+"F1.imprint","IMPRINT",FACE,{"disambiguationData":[TD([[makeQuery(id+"F1.imprint","IMPRINT",EDGE,{"derivedFrom":subQ7}),-1.0]])]});}
            var Q24;
            {var subQ2=sQuery(id+"F1.wireOp",EDGE,"E52.2.15.0");Q24=makeQuery(id+"F1.imprint","IMPRINT",FACE,{"disambiguationData":[TD([[makeQuery(id+"F1.imprint","IMPRINT",EDGE,{"derivedFrom":subQ2}),-1.0]])]});}
            var Q25;
            {var subQ6=sQuery(id+"F1.wireOp",EDGE,"E52.2.16.0");Q25=makeQuery(id+"F1.imprint","IMPRINT",FACE,{"disambiguationData":[TD([[makeQuery(id+"F1.imprint","IMPRINT",EDGE,{"derivedFrom":subQ6}),-1.0]])]});}
            var Q26;
            {var subQ2=sQuery(id+"F1.wireOp",EDGE,"E52.2.17.0");Q26=makeQuery(id+"F1.imprint","IMPRINT",FACE,{"disambiguationData":[TD([[makeQuery(id+"F1.imprint","IMPRINT",EDGE,{"derivedFrom":subQ2}),-1.0]])]});}
            var Q27;
            {var subQ0=sQuery(id+"F1.wireOp",EDGE,"E52.2.18.0");Q27=makeQuery(id+"F1.imprint","IMPRINT",FACE,{"disambiguationData":[TD([[makeQuery(id+"F1.imprint","IMPRINT",EDGE,{"derivedFrom":subQ0}),-1.0]])]});}
            var Q28;
            {var subQ2=sQuery(id+"F1.wireOp",EDGE,"E52.2.19.0");Q28=makeQuery(id+"F1.imprint","IMPRINT",FACE,{"disambiguationData":[TD([[makeQuery(id+"F1.imprint","IMPRINT",EDGE,{"derivedFrom":subQ2}),-1.0]])]});}
            extrude(context, id + "F2", {"entities" : qUnion([Q0, Q1, Q2, Q3, Q4, Q5, Q6, Q7, Q8, Q9, Q10, Q11, Q12, Q13, Q14, Q15, Q16, Q17, Q18, Q19, Q20, Q21, Q22, Q23, Q24, Q25, Q26, Q27, Q28]), "depth" : (getVariable(context, 'GearThickness')) * mm});
        }
        {
            var Q0;
            Q0=makeQuery(id+"F2.opExtrude","CAP_FACE",FACE,{"disambiguationData":[OSD([sQuery(id+"F1.wireOp",EDGE,"E0"),sQuery(id+"F1.wireOp",EDGE,"E3"),sQuery(id+"F1.wireOp",EDGE,"E21"),sQuery(id+"F1.wireOp",EDGE,"E22.MirrorCS"),sQuery(id+"F1.wireOp",EDGE,"E23"),sQuery(id+"F1.wireOp",EDGE,"E24"),sQuery(id+"F1.wireOp",EDGE,"E25"),sQuery(id+"F1.wireOp",EDGE,"E26"),sQuery(id+"F1.wireOp",EDGE,"E27"),sQuery(id+"F1.wireOp",EDGE,"E28"),sQuery(id+"F1.wireOp",EDGE,"E29"),sQuery(id+"F1.wireOp",EDGE,"E30"),sQuery(id+"F1.wireOp",EDGE,"E31"),sQuery(id+"F1.wireOp",EDGE,"E32"),sQuery(id+"F1.wireOp",EDGE,"E33"),sQuery(id+"F1.wireOp",EDGE,"E34"),sQuery(id+"F1.wireOp",EDGE,"E35"),sQuery(id+"F1.wireOp",EDGE,"E36"),sQuery(id+"F1.wireOp",EDGE,"E37.MirrorCS"),sQuery(id+"F1.wireOp",EDGE,"E38.MirrorCS"),sQuery(id+"F1.wireOp",EDGE,"E39.MirrorCS"),sQuery(id+"F1.wireOp",EDGE,"E40.MirrorCS"),sQuery(id+"F1.wireOp",EDGE,"E41.MirrorCS"),sQuery(id+"F1.wireOp",EDGE,"E42.MirrorCS"),sQuery(id+"F1.wireOp",EDGE,"E43.MirrorCS"),sQuery(id+"F1.wireOp",EDGE,"E44.MirrorCS"),sQuery(id+"F1.wireOp",EDGE,"E45.MirrorCS"),sQuery(id+"F1.wireOp",EDGE,"E46.MirrorCS"),sQuery(id+"F1.wireOp",EDGE,"E47.MirrorCS"),sQuery(id+"F1.wireOp",EDGE,"E48.MirrorCS"),sQuery(id+"F1.wireOp",EDGE,"E49.MirrorCS"),sQuery(id+"F1.wireOp",EDGE,"E50.MirrorCS"),sQuery(id+"F1.wireOp",EDGE,"E51.1.0"),sQuery(id+"F1.wireOp",EDGE,"E51.1.1"),sQuery(id+"F1.wireOp",EDGE,"E51.1.2"),sQuery(id+"F1.wireOp",EDGE,"E51.1.3"),sQuery(id+"F1.wireOp",EDGE,"E51.1.4"),sQuery(id+"F1.wireOp",EDGE,"E51.1.5"),sQuery(id+"F1.wireOp",EDGE,"E51.1.6"),sQuery(id+"F1.wireOp",EDGE,"E51.1.7"),sQuery(id+"F1.wireOp",EDGE,"E51.1.8"),sQuery(id+"F1.wireOp",EDGE,"E51.1.9"),sQuery(id+"F1.wireOp",EDGE,"E51.1.10"),sQuery(id+"F1.wireOp",EDGE,"E51.1.11"),sQuery(id+"F1.wireOp",EDGE,"E51.1.12"),sQuery(id+"F1.wireOp",EDGE,"E51.1.13"),sQuery(id+"F1.wireOp",EDGE,"E51.1.14"),sQuery(id+"F1.wireOp",EDGE,"E51.1.15"),sQuery(id+"F1.wireOp",EDGE,"E51.1.16"),sQuery(id+"F1.wireOp",EDGE,"E51.1.17"),sQuery(id+"F1.wireOp",EDGE,"E51.1.18"),sQuery(id+"F1.wireOp",EDGE,"E51.1.19"),sQuery(id+"F1.wireOp",EDGE,"E51.1.20"),sQuery(id+"F1.wireOp",EDGE,"E51.1.21"),sQuery(id+"F1.wireOp",EDGE,"E51.1.22"),sQuery(id+"F1.wireOp",EDGE,"E51.1.23"),sQuery(id+"F1.wireOp",EDGE,"E51.1.24"),sQuery(id+"F1.wireOp",EDGE,"E51.1.25"),sQuery(id+"F1.wireOp",EDGE,"E51.1.26"),sQuery(id+"F1.wireOp",EDGE,"E51.1.27"),sQuery(id+"F1.wireOp",EDGE,"E51.1.28"),sQuery(id+"F1.wireOp",EDGE,"E51.1.29"),sQuery(id+"F1.wireOp",EDGE,"E51.2.0"),sQuery(id+"F1.wireOp",EDGE,"E51.2.1"),sQuery(id+"F1.wireOp",EDGE,"E51.2.2"),sQuery(id+"F1.wireOp",EDGE,"E51.2.3"),sQuery(id+"F1.wireOp",EDGE,"E51.2.4"),sQuery(id+"F1.wireOp",EDGE,"E51.2.5"),sQuery(id+"F1.wireOp",EDGE,"E51.2.6"),sQuery(id+"F1.wireOp",EDGE,"E51.2.7"),sQuery(id+"F1.wireOp",EDGE,"E51.2.8"),sQuery(id+"F1.wireOp",EDGE,"E51.2.9"),sQuery(id+"F1.wireOp",EDGE,"E51.2.10"),sQuery(id+"F1.wireOp",EDGE,"E51.2.11"),sQuery(id+"F1.wireOp",EDGE,"E51.2.12"),sQuery(id+"F1.wireOp",EDGE,"E51.2.13"),sQuery(id+"F1.wireOp",EDGE,"E51.2.14"),sQuery(id+"F1.wireOp",EDGE,"E51.2.15"),sQuery(id+"F1.wireOp",EDGE,"E51.2.16"),sQuery(id+"F1.wireOp",EDGE,"E51.2.17"),sQuery(id+"F1.wireOp",EDGE,"E51.2.18"),sQuery(id+"F1.wireOp",EDGE,"E51.2.19"),sQuery(id+"F1.wireOp",EDGE,"E51.2.20"),sQuery(id+"F1.wireOp",EDGE,"E51.2.21"),sQuery(id+"F1.wireOp",EDGE,"E51.2.22"),sQuery(id+"F1.wireOp",EDGE,"E51.2.23"),sQuery(id+"F1.wireOp",EDGE,"E51.2.24"),sQuery(id+"F1.wireOp",EDGE,"E51.2.25"),sQuery(id+"F1.wireOp",EDGE,"E51.2.26"),sQuery(id+"F1.wireOp",EDGE,"E51.2.27"),sQuery(id+"F1.wireOp",EDGE,"E51.2.28"),sQuery(id+"F1.wireOp",EDGE,"E51.2.29"),sQuery(id+"F1.wireOp",EDGE,"E51.3.0"),sQuery(id+"F1.wireOp",EDGE,"E51.3.1"),sQuery(id+"F1.wireOp",EDGE,"E51.3.2"),sQuery(id+"F1.wireOp",EDGE,"E51.3.3"),sQuery(id+"F1.wireOp",EDGE,"E51.3.4"),sQuery(id+"F1.wireOp",EDGE,"E51.3.5"),sQuery(id+"F1.wireOp",EDGE,"E51.3.6"),sQuery(id+"F1.wireOp",EDGE,"E51.3.7"),sQuery(id+"F1.wireOp",EDGE,"E51.3.8"),sQuery(id+"F1.wireOp",EDGE,"E51.3.9"),sQuery(id+"F1.wireOp",EDGE,"E51.3.10"),sQuery(id+"F1.wireOp",EDGE,"E51.3.11"),sQuery(id+"F1.wireOp",EDGE,"E51.3.12"),sQuery(id+"F1.wireOp",EDGE,"E51.3.13"),sQuery(id+"F1.wireOp",EDGE,"E51.3.14"),sQuery(id+"F1.wireOp",EDGE,"E51.3.15"),sQuery(id+"F1.wireOp",EDGE,"E51.3.16"),sQuery(id+"F1.wireOp",EDGE,"E51.3.17"),sQuery(id+"F1.wireOp",EDGE,"E51.3.18"),sQuery(id+"F1.wireOp",EDGE,"E51.3.19"),sQuery(id+"F1.wireOp",EDGE,"E51.3.20"),sQuery(id+"F1.wireOp",EDGE,"E51.3.21"),sQuery(id+"F1.wireOp",EDGE,"E51.3.22"),sQuery(id+"F1.wireOp",EDGE,"E51.3.23"),sQuery(id+"F1.wireOp",EDGE,"E51.3.24"),sQuery(id+"F1.wireOp",EDGE,"E51.3.25"),sQuery(id+"F1.wireOp",EDGE,"E51.3.26"),sQuery(id+"F1.wireOp",EDGE,"E51.3.27"),sQuery(id+"F1.wireOp",EDGE,"E51.3.28"),sQuery(id+"F1.wireOp",EDGE,"E51.3.29"),sQuery(id+"F1.wireOp",EDGE,"E51.4.0"),sQuery(id+"F1.wireOp",EDGE,"E51.4.1"),sQuery(id+"F1.wireOp",EDGE,"E51.4.2"),sQuery(id+"F1.wireOp",EDGE,"E51.4.3"),sQuery(id+"F1.wireOp",EDGE,"E51.4.4"),sQuery(id+"F1.wireOp",EDGE,"E51.4.5"),sQuery(id+"F1.wireOp",EDGE,"E51.4.6"),sQuery(id+"F1.wireOp",EDGE,"E51.4.7"),sQuery(id+"F1.wireOp",EDGE,"E51.4.8"),sQuery(id+"F1.wireOp",EDGE,"E51.4.9"),sQuery(id+"F1.wireOp",EDGE,"E51.4.10"),sQuery(id+"F1.wireOp",EDGE,"E51.4.11"),sQuery(id+"F1.wireOp",EDGE,"E51.4.12"),sQuery(id+"F1.wireOp",EDGE,"E51.4.13"),sQuery(id+"F1.wireOp",EDGE,"E51.4.14"),sQuery(id+"F1.wireOp",EDGE,"E51.4.15"),sQuery(id+"F1.wireOp",EDGE,"E51.4.16"),sQuery(id+"F1.wireOp",EDGE,"E51.4.17"),sQuery(id+"F1.wireOp",EDGE,"E51.4.18"),sQuery(id+"F1.wireOp",EDGE,"E51.4.19"),sQuery(id+"F1.wireOp",EDGE,"E51.4.20"),sQuery(id+"F1.wireOp",EDGE,"E51.4.21"),sQuery(id+"F1.wireOp",EDGE,"E51.4.22"),sQuery(id+"F1.wireOp",EDGE,"E51.4.23"),sQuery(id+"F1.wireOp",EDGE,"E51.4.24"),sQuery(id+"F1.wireOp",EDGE,"E51.4.25"),sQuery(id+"F1.wireOp",EDGE,"E51.4.26"),sQuery(id+"F1.wireOp",EDGE,"E51.4.27"),sQuery(id+"F1.wireOp",EDGE,"E51.4.28"),sQuery(id+"F1.wireOp",EDGE,"E51.4.29"),sQuery(id+"F1.wireOp",EDGE,"E51.5.0"),sQuery(id+"F1.wireOp",EDGE,"E51.5.1"),sQuery(id+"F1.wireOp",EDGE,"E51.5.2"),sQuery(id+"F1.wireOp",EDGE,"E51.5.3"),sQuery(id+"F1.wireOp",EDGE,"E51.5.4"),sQuery(id+"F1.wireOp",EDGE,"E51.5.5"),sQuery(id+"F1.wireOp",EDGE,"E51.5.6"),sQuery(id+"F1.wireOp",EDGE,"E51.5.7"),sQuery(id+"F1.wireOp",EDGE,"E51.5.8"),sQuery(id+"F1.wireOp",EDGE,"E51.5.9"),sQuery(id+"F1.wireOp",EDGE,"E51.5.10"),sQuery(id+"F1.wireOp",EDGE,"E51.5.11"),sQuery(id+"F1.wireOp",EDGE,"E51.5.12"),sQuery(id+"F1.wireOp",EDGE,"E51.5.13"),sQuery(id+"F1.wireOp",EDGE,"E51.5.14"),sQuery(id+"F1.wireOp",EDGE,"E51.5.15"),sQuery(id+"F1.wireOp",EDGE,"E51.5.16"),sQuery(id+"F1.wireOp",EDGE,"E51.5.17"),sQuery(id+"F1.wireOp",EDGE,"E51.5.18"),sQuery(id+"F1.wireOp",EDGE,"E51.5.19"),sQuery(id+"F1.wireOp",EDGE,"E51.5.20"),sQuery(id+"F1.wireOp",EDGE,"E51.5.21"),sQuery(id+"F1.wireOp",EDGE,"E51.5.22"),sQuery(id+"F1.wireOp",EDGE,"E51.5.23"),sQuery(id+"F1.wireOp",EDGE,"E51.5.24"),sQuery(id+"F1.wireOp",EDGE,"E51.5.25"),sQuery(id+"F1.wireOp",EDGE,"E51.5.26"),sQuery(id+"F1.wireOp",EDGE,"E51.5.27"),sQuery(id+"F1.wireOp",EDGE,"E51.5.28"),sQuery(id+"F1.wireOp",EDGE,"E51.5.29"),sQuery(id+"F1.wireOp",EDGE,"E51.6.0"),sQuery(id+"F1.wireOp",EDGE,"E51.6.1"),sQuery(id+"F1.wireOp",EDGE,"E51.6.2"),sQuery(id+"F1.wireOp",EDGE,"E51.6.3"),sQuery(id+"F1.wireOp",EDGE,"E51.6.4"),sQuery(id+"F1.wireOp",EDGE,"E51.6.5"),sQuery(id+"F1.wireOp",EDGE,"E51.6.6"),sQuery(id+"F1.wireOp",EDGE,"E51.6.7"),sQuery(id+"F1.wireOp",EDGE,"E51.6.8"),sQuery(id+"F1.wireOp",EDGE,"E51.6.9"),sQuery(id+"F1.wireOp",EDGE,"E51.6.10"),sQuery(id+"F1.wireOp",EDGE,"E51.6.11"),sQuery(id+"F1.wireOp",EDGE,"E51.6.12"),sQuery(id+"F1.wireOp",EDGE,"E51.6.13"),sQuery(id+"F1.wireOp",EDGE,"E51.6.14"),sQuery(id+"F1.wireOp",EDGE,"E51.6.15"),sQuery(id+"F1.wireOp",EDGE,"E51.6.16"),sQuery(id+"F1.wireOp",EDGE,"E51.6.17"),sQuery(id+"F1.wireOp",EDGE,"E51.6.18"),sQuery(id+"F1.wireOp",EDGE,"E51.6.19"),sQuery(id+"F1.wireOp",EDGE,"E51.6.20"),sQuery(id+"F1.wireOp",EDGE,"E51.6.21"),sQuery(id+"F1.wireOp",EDGE,"E51.6.22"),sQuery(id+"F1.wireOp",EDGE,"E51.6.23"),sQuery(id+"F1.wireOp",EDGE,"E51.6.24"),sQuery(id+"F1.wireOp",EDGE,"E51.6.25"),sQuery(id+"F1.wireOp",EDGE,"E51.6.26"),sQuery(id+"F1.wireOp",EDGE,"E51.6.27"),sQuery(id+"F1.wireOp",EDGE,"E51.6.28"),sQuery(id+"F1.wireOp",EDGE,"E51.6.29"),sQuery(id+"F1.wireOp",EDGE,"E51.7.0"),sQuery(id+"F1.wireOp",EDGE,"E51.7.1"),sQuery(id+"F1.wireOp",EDGE,"E51.7.2"),sQuery(id+"F1.wireOp",EDGE,"E51.7.3"),sQuery(id+"F1.wireOp",EDGE,"E51.7.4"),sQuery(id+"F1.wireOp",EDGE,"E51.7.5"),sQuery(id+"F1.wireOp",EDGE,"E51.7.6"),sQuery(id+"F1.wireOp",EDGE,"E51.7.7"),sQuery(id+"F1.wireOp",EDGE,"E51.7.8"),sQuery(id+"F1.wireOp",EDGE,"E51.7.9"),sQuery(id+"F1.wireOp",EDGE,"E51.7.10"),sQuery(id+"F1.wireOp",EDGE,"E51.7.11"),sQuery(id+"F1.wireOp",EDGE,"E51.7.12"),sQuery(id+"F1.wireOp",EDGE,"E51.7.13"),sQuery(id+"F1.wireOp",EDGE,"E51.7.14"),sQuery(id+"F1.wireOp",EDGE,"E51.7.15"),sQuery(id+"F1.wireOp",EDGE,"E51.7.16"),sQuery(id+"F1.wireOp",EDGE,"E51.7.17"),sQuery(id+"F1.wireOp",EDGE,"E51.7.18"),sQuery(id+"F1.wireOp",EDGE,"E51.7.19"),sQuery(id+"F1.wireOp",EDGE,"E51.7.20"),sQuery(id+"F1.wireOp",EDGE,"E51.7.21"),sQuery(id+"F1.wireOp",EDGE,"E51.7.22"),sQuery(id+"F1.wireOp",EDGE,"E51.7.23"),sQuery(id+"F1.wireOp",EDGE,"E51.7.24"),sQuery(id+"F1.wireOp",EDGE,"E51.7.25"),sQuery(id+"F1.wireOp",EDGE,"E51.7.26"),sQuery(id+"F1.wireOp",EDGE,"E51.7.27"),sQuery(id+"F1.wireOp",EDGE,"E51.7.28"),sQuery(id+"F1.wireOp",EDGE,"E51.7.29"),sQuery(id+"F1.wireOp",EDGE,"E51.8.0"),sQuery(id+"F1.wireOp",EDGE,"E51.8.1"),sQuery(id+"F1.wireOp",EDGE,"E51.8.2"),sQuery(id+"F1.wireOp",EDGE,"E51.8.3"),sQuery(id+"F1.wireOp",EDGE,"E51.8.4"),sQuery(id+"F1.wireOp",EDGE,"E51.8.5"),sQuery(id+"F1.wireOp",EDGE,"E51.8.6"),sQuery(id+"F1.wireOp",EDGE,"E51.8.7"),sQuery(id+"F1.wireOp",EDGE,"E51.8.8"),sQuery(id+"F1.wireOp",EDGE,"E51.8.9"),sQuery(id+"F1.wireOp",EDGE,"E51.8.10"),sQuery(id+"F1.wireOp",EDGE,"E51.8.11"),sQuery(id+"F1.wireOp",EDGE,"E51.8.12"),sQuery(id+"F1.wireOp",EDGE,"E51.8.13"),sQuery(id+"F1.wireOp",EDGE,"E51.8.14"),sQuery(id+"F1.wireOp",EDGE,"E51.8.15"),sQuery(id+"F1.wireOp",EDGE,"E51.8.16"),sQuery(id+"F1.wireOp",EDGE,"E51.8.17"),sQuery(id+"F1.wireOp",EDGE,"E51.8.18"),sQuery(id+"F1.wireOp",EDGE,"E51.8.19"),sQuery(id+"F1.wireOp",EDGE,"E51.8.20"),sQuery(id+"F1.wireOp",EDGE,"E51.8.21"),sQuery(id+"F1.wireOp",EDGE,"E51.8.22"),sQuery(id+"F1.wireOp",EDGE,"E51.8.23"),sQuery(id+"F1.wireOp",EDGE,"E51.8.24"),sQuery(id+"F1.wireOp",EDGE,"E51.8.25"),sQuery(id+"F1.wireOp",EDGE,"E51.8.26"),sQuery(id+"F1.wireOp",EDGE,"E51.8.27"),sQuery(id+"F1.wireOp",EDGE,"E51.8.28"),sQuery(id+"F1.wireOp",EDGE,"E51.8.29"),sQuery(id+"F1.wireOp",EDGE,"E51.9.0"),sQuery(id+"F1.wireOp",EDGE,"E51.9.1"),sQuery(id+"F1.wireOp",EDGE,"E51.9.2"),sQuery(id+"F1.wireOp",EDGE,"E51.9.3"),sQuery(id+"F1.wireOp",EDGE,"E51.9.4"),sQuery(id+"F1.wireOp",EDGE,"E51.9.5"),sQuery(id+"F1.wireOp",EDGE,"E51.9.6"),sQuery(id+"F1.wireOp",EDGE,"E51.9.7"),sQuery(id+"F1.wireOp",EDGE,"E51.9.8"),sQuery(id+"F1.wireOp",EDGE,"E51.9.9"),sQuery(id+"F1.wireOp",EDGE,"E51.9.10"),sQuery(id+"F1.wireOp",EDGE,"E51.9.11"),sQuery(id+"F1.wireOp",EDGE,"E51.9.12"),sQuery(id+"F1.wireOp",EDGE,"E51.9.13"),sQuery(id+"F1.wireOp",EDGE,"E51.9.14"),sQuery(id+"F1.wireOp",EDGE,"E51.9.15"),sQuery(id+"F1.wireOp",EDGE,"E51.9.16"),sQuery(id+"F1.wireOp",EDGE,"E51.9.17"),sQuery(id+"F1.wireOp",EDGE,"E51.9.18"),sQuery(id+"F1.wireOp",EDGE,"E51.9.19"),sQuery(id+"F1.wireOp",EDGE,"E51.9.20"),sQuery(id+"F1.wireOp",EDGE,"E51.9.21"),sQuery(id+"F1.wireOp",EDGE,"E51.9.22"),sQuery(id+"F1.wireOp",EDGE,"E51.9.23"),sQuery(id+"F1.wireOp",EDGE,"E51.9.24"),sQuery(id+"F1.wireOp",EDGE,"E51.9.25"),sQuery(id+"F1.wireOp",EDGE,"E51.9.26"),sQuery(id+"F1.wireOp",EDGE,"E51.9.27"),sQuery(id+"F1.wireOp",EDGE,"E51.9.28"),sQuery(id+"F1.wireOp",EDGE,"E51.9.29"),sQuery(id+"F1.wireOp",EDGE,"E51.10.0"),sQuery(id+"F1.wireOp",EDGE,"E51.10.1"),sQuery(id+"F1.wireOp",EDGE,"E51.10.2"),sQuery(id+"F1.wireOp",EDGE,"E51.10.3"),sQuery(id+"F1.wireOp",EDGE,"E51.10.4"),sQuery(id+"F1.wireOp",EDGE,"E51.10.5"),sQuery(id+"F1.wireOp",EDGE,"E51.10.6"),sQuery(id+"F1.wireOp",EDGE,"E51.10.7"),sQuery(id+"F1.wireOp",EDGE,"E51.10.8"),sQuery(id+"F1.wireOp",EDGE,"E51.10.9"),sQuery(id+"F1.wireOp",EDGE,"E51.10.10"),sQuery(id+"F1.wireOp",EDGE,"E51.10.11"),sQuery(id+"F1.wireOp",EDGE,"E51.10.12"),sQuery(id+"F1.wireOp",EDGE,"E51.10.13"),sQuery(id+"F1.wireOp",EDGE,"E51.10.14"),sQuery(id+"F1.wireOp",EDGE,"E51.10.15"),sQuery(id+"F1.wireOp",EDGE,"E51.10.16"),sQuery(id+"F1.wireOp",EDGE,"E51.10.17"),sQuery(id+"F1.wireOp",EDGE,"E51.10.18"),sQuery(id+"F1.wireOp",EDGE,"E51.10.19"),sQuery(id+"F1.wireOp",EDGE,"E51.10.20"),sQuery(id+"F1.wireOp",EDGE,"E51.10.21"),sQuery(id+"F1.wireOp",EDGE,"E51.10.22"),sQuery(id+"F1.wireOp",EDGE,"E51.10.23"),sQuery(id+"F1.wireOp",EDGE,"E51.10.24"),sQuery(id+"F1.wireOp",EDGE,"E51.10.25"),sQuery(id+"F1.wireOp",EDGE,"E51.10.26"),sQuery(id+"F1.wireOp",EDGE,"E51.10.27"),sQuery(id+"F1.wireOp",EDGE,"E51.10.28"),sQuery(id+"F1.wireOp",EDGE,"E51.10.29"),sQuery(id+"F1.wireOp",EDGE,"E51.11.0"),sQuery(id+"F1.wireOp",EDGE,"E51.11.1"),sQuery(id+"F1.wireOp",EDGE,"E51.11.2"),sQuery(id+"F1.wireOp",EDGE,"E51.11.3"),sQuery(id+"F1.wireOp",EDGE,"E51.11.4"),sQuery(id+"F1.wireOp",EDGE,"E51.11.5"),sQuery(id+"F1.wireOp",EDGE,"E51.11.6"),sQuery(id+"F1.wireOp",EDGE,"E51.11.7"),sQuery(id+"F1.wireOp",EDGE,"E51.11.8"),sQuery(id+"F1.wireOp",EDGE,"E51.11.9"),sQuery(id+"F1.wireOp",EDGE,"E51.11.10"),sQuery(id+"F1.wireOp",EDGE,"E51.11.11"),sQuery(id+"F1.wireOp",EDGE,"E51.11.12"),sQuery(id+"F1.wireOp",EDGE,"E51.11.13"),sQuery(id+"F1.wireOp",EDGE,"E51.11.14"),sQuery(id+"F1.wireOp",EDGE,"E51.11.15"),sQuery(id+"F1.wireOp",EDGE,"E51.11.16"),sQuery(id+"F1.wireOp",EDGE,"E51.11.17"),sQuery(id+"F1.wireOp",EDGE,"E51.11.18"),sQuery(id+"F1.wireOp",EDGE,"E51.11.19"),sQuery(id+"F1.wireOp",EDGE,"E51.11.20"),sQuery(id+"F1.wireOp",EDGE,"E51.11.21"),sQuery(id+"F1.wireOp",EDGE,"E51.11.22"),sQuery(id+"F1.wireOp",EDGE,"E51.11.23"),sQuery(id+"F1.wireOp",EDGE,"E51.11.24"),sQuery(id+"F1.wireOp",EDGE,"E51.11.25"),sQuery(id+"F1.wireOp",EDGE,"E51.11.26"),sQuery(id+"F1.wireOp",EDGE,"E51.11.27"),sQuery(id+"F1.wireOp",EDGE,"E51.11.28"),sQuery(id+"F1.wireOp",EDGE,"E51.11.29")])],"isStart":true});
            var sketch = newSketch(context, id + "F3", { "sketchPlane" : qUnion([Q0])});
            skCircle(sketch, "E53", {"center": v(0, 0) * mm, "radius": 5 * mm});
            skSolve(sketch);
        }
        {
            var Q0;
            Q0=makeQuery(id+"F3.imprint","IMPRINT",FACE,{"disambiguationData":[TD([[makeQuery(id+"F3.imprint","IMPRINT",EDGE,{"derivedFrom":sQuery(id+"F3.wireOp",EDGE,"E53")}),1.0]])]});
            var Q1;
            Q1=sQuery(id+"F3.wireOp",EDGE,"E53");
            extrude(context, id + "F4", {"entities" : qUnion([Q0]), "operationType" : NewBodyOperationType.REMOVE, "surfaceEntities" : qUnion([Q1]), "endBound" : BoundingType.THROUGH_ALL, "oppositeDirection" : true, "depth" : 25 * mm});
        }
        {
            var Q0;
            Q0=qCreatedBy(makeId("Right.planeOp"),FACE);
            var sketch = newSketch(context, id + "F5", { "sketchPlane" : qUnion([Q0])});
            skCircle(sketch, "E54", {"center": v(0, 0) * mm, "radius": 18 * mm, "construction": true});
            skCircle(sketch, "E55", {"center": v(0, 0) * mm, "radius": 8 * mm, "construction": true});
            skLineSegment(sketch, "E56", {"start": v(5.66, 5.66) * mm, "end": v(12.73, 12.73) * mm});
            skLineSegment(sketch, "E57", {"start": v(-5.66, 5.66) * mm, "end": v(-12.73, 12.73) * mm});
            skArc(sketch, "E58", {"start": v(12.73, 12.73) * mm, "mid": v(0, 18) * mm, "end": v(-12.73, 12.73) * mm});
            skArc(sketch, "E59", {"start": v(5.66, 5.66) * mm, "mid": v(0, 8) * mm, "end": v(-5.66, 5.66) * mm});
            skArc(sketch, "E60.1.0", {"start": v(-7.73, 2.07) * mm, "mid": v(-6.93, -4) * mm, "end": v(-2.07, -7.73) * mm});
            skArc(sketch, "E60.1.1", {"start": v(-17.39, 4.66) * mm, "mid": v(-15.59, -9) * mm, "end": v(-4.66, -17.39) * mm});
            skLineSegment(sketch, "E60.1.2", {"start": v(-2.07, -7.73) * mm, "end": v(-4.66, -17.39) * mm});
            skLineSegment(sketch, "E60.1.3", {"start": v(-7.73, 2.07) * mm, "end": v(-17.39, 4.66) * mm});
            skArc(sketch, "E60.2.0", {"start": v(2.07, -7.73) * mm, "mid": v(6.93, -4) * mm, "end": v(7.73, 2.07) * mm});
            skArc(sketch, "E60.2.1", {"start": v(4.66, -17.39) * mm, "mid": v(15.59, -9) * mm, "end": v(17.39, 4.66) * mm});
            skLineSegment(sketch, "E60.2.2", {"start": v(7.73, 2.07) * mm, "end": v(17.39, 4.66) * mm});
            skLineSegment(sketch, "E60.2.3", {"start": v(2.07, -7.73) * mm, "end": v(4.66, -17.39) * mm});
            skSolve(sketch);
        }
        {
            var Q0;
            Q0 = qSketchRegion(id + "F5", true);
            extrude(context, id + "F6", {"entities" : qUnion([Q0]), "operationType" : NewBodyOperationType.REMOVE, "depth" : 25 * mm});
        }
        {
            var Q0;
            Q0=makeQuery(id+"F6.boolean.opBoolean","COPY",EDGE,{"derivedFrom":makeQuery(id+"F6.opExtrude","SWEPT_EDGE",EDGE,{"disambiguationData":[OSD([sQuery(id+"F5.wireOp",EDGE,"E57"),sQuery(id+"F5.wireOp",EDGE,"E58")])]})});
            var Q1;
            Q1=makeQuery(id+"F6.boolean.opBoolean","COPY",EDGE,{"derivedFrom":makeQuery(id+"F6.opExtrude","SWEPT_EDGE",EDGE,{"disambiguationData":[OSD([sQuery(id+"F5.wireOp",EDGE,"E57"),sQuery(id+"F5.wireOp",EDGE,"E59")])]})});
            var Q2;
            Q2=makeQuery(id+"F6.boolean.opBoolean","COPY",EDGE,{"derivedFrom":makeQuery(id+"F6.opExtrude","SWEPT_EDGE",EDGE,{"disambiguationData":[OSD([sQuery(id+"F5.wireOp",EDGE,"E56"),sQuery(id+"F5.wireOp",EDGE,"E59")])]})});
            var Q3;
            Q3=makeQuery(id+"F6.boolean.opBoolean","COPY",EDGE,{"derivedFrom":makeQuery(id+"F6.opExtrude","SWEPT_EDGE",EDGE,{"disambiguationData":[OSD([sQuery(id+"F5.wireOp",EDGE,"E56"),sQuery(id+"F5.wireOp",EDGE,"E58")])]})});
            var Q4;
            Q4=makeQuery(id+"F6.boolean.opBoolean","COPY",EDGE,{"derivedFrom":makeQuery(id+"F6.opExtrude","SWEPT_EDGE",EDGE,{"disambiguationData":[OSD([sQuery(id+"F5.wireOp",EDGE,"E60.2.0"),sQuery(id+"F5.wireOp",EDGE,"E60.2.2")])]})});
            var Q5;
            Q5=makeQuery(id+"F6.boolean.opBoolean","COPY",EDGE,{"derivedFrom":makeQuery(id+"F6.opExtrude","SWEPT_EDGE",EDGE,{"disambiguationData":[OSD([sQuery(id+"F5.wireOp",EDGE,"E60.2.0"),sQuery(id+"F5.wireOp",EDGE,"E60.2.3")])]})});
            var Q6;
            Q6=makeQuery(id+"F6.boolean.opBoolean","COPY",EDGE,{"derivedFrom":makeQuery(id+"F6.opExtrude","SWEPT_EDGE",EDGE,{"disambiguationData":[OSD([sQuery(id+"F5.wireOp",EDGE,"E60.1.0"),sQuery(id+"F5.wireOp",EDGE,"E60.1.2")])]})});
            var Q7;
            Q7=makeQuery(id+"F6.boolean.opBoolean","COPY",EDGE,{"derivedFrom":makeQuery(id+"F6.opExtrude","SWEPT_EDGE",EDGE,{"disambiguationData":[OSD([sQuery(id+"F5.wireOp",EDGE,"E60.1.0"),sQuery(id+"F5.wireOp",EDGE,"E60.1.3")])]})});
            var Q8;
            Q8=makeQuery(id+"F6.boolean.opBoolean","COPY",EDGE,{"derivedFrom":makeQuery(id+"F6.opExtrude","SWEPT_EDGE",EDGE,{"disambiguationData":[OSD([sQuery(id+"F5.wireOp",EDGE,"E60.1.1"),sQuery(id+"F5.wireOp",EDGE,"E60.1.3")])]})});
            var Q9;
            Q9=makeQuery(id+"F6.boolean.opBoolean","COPY",EDGE,{"derivedFrom":makeQuery(id+"F6.opExtrude","SWEPT_EDGE",EDGE,{"disambiguationData":[OSD([sQuery(id+"F5.wireOp",EDGE,"E60.1.1"),sQuery(id+"F5.wireOp",EDGE,"E60.1.2")])]})});
            var Q10;
            Q10=makeQuery(id+"F6.boolean.opBoolean","COPY",EDGE,{"derivedFrom":makeQuery(id+"F6.opExtrude","SWEPT_EDGE",EDGE,{"disambiguationData":[OSD([sQuery(id+"F5.wireOp",EDGE,"E60.2.1"),sQuery(id+"F5.wireOp",EDGE,"E60.2.3")])]})});
            var Q11;
            Q11=makeQuery(id+"F6.boolean.opBoolean","COPY",EDGE,{"derivedFrom":makeQuery(id+"F6.opExtrude","SWEPT_EDGE",EDGE,{"disambiguationData":[OSD([sQuery(id+"F5.wireOp",EDGE,"E60.2.1"),sQuery(id+"F5.wireOp",EDGE,"E60.2.2")])]})});
            fillet(context, id + "F7", {"entities" : qUnion([Q0, Q1, Q2, Q3, Q4, Q5, Q6, Q7, Q8, Q9, Q10, Q11]), "radius" : 3 * mm, "tangentPropagation" : true, "allowEdgeOverflow" : false});
        }
    });
